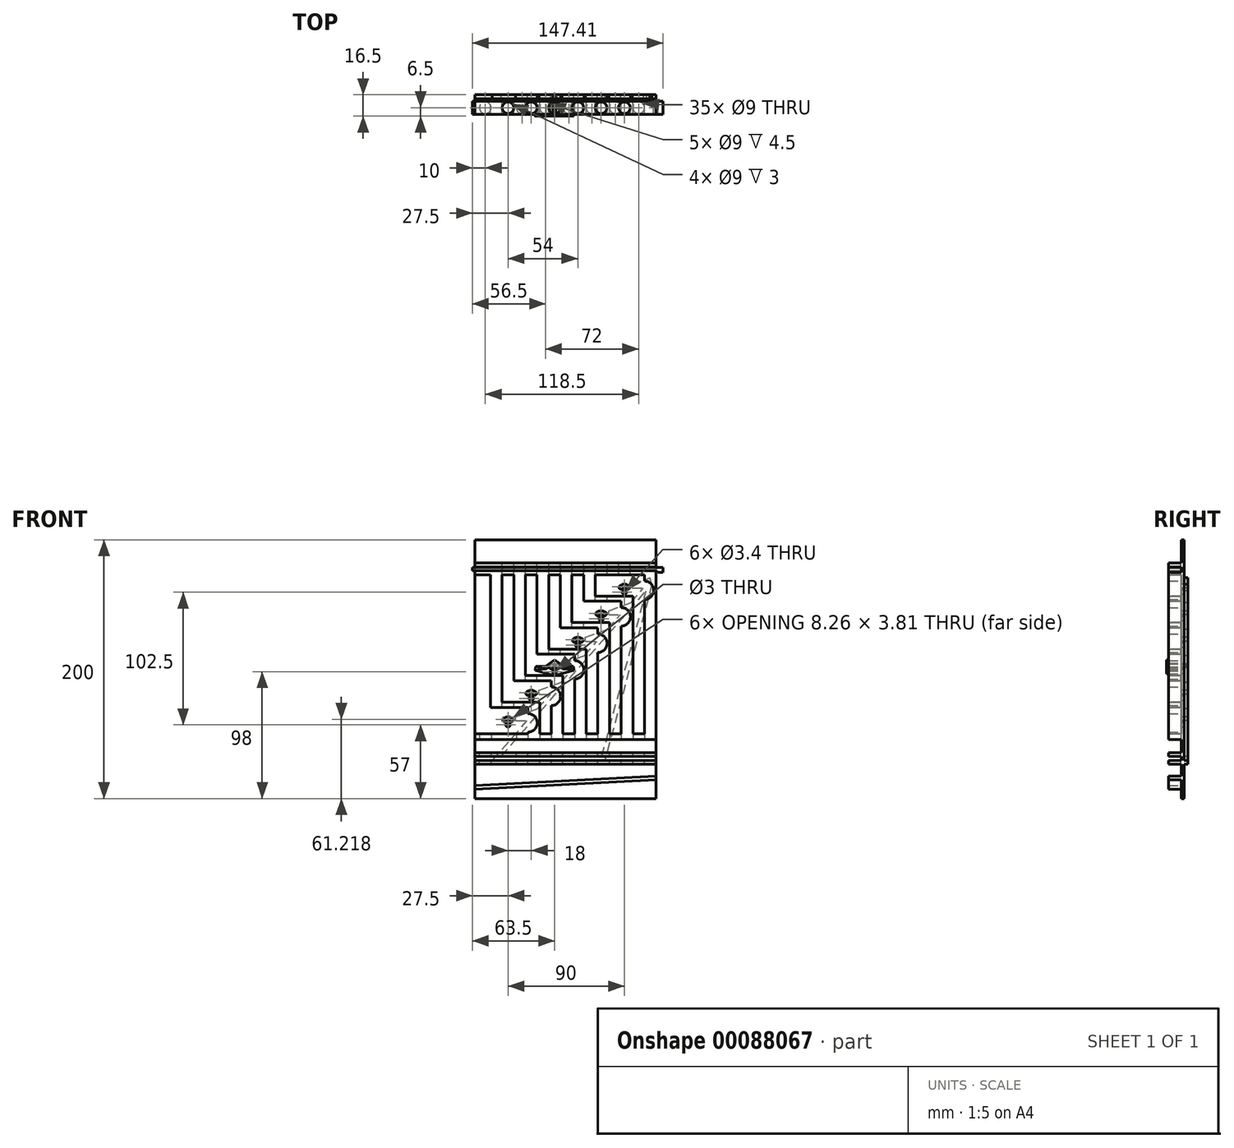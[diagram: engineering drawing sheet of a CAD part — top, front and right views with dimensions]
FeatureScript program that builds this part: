
annotation { "Feature Type Name" : "Feature", "Feature Type Description" : "" }
export const myFeature = defineFeature(function(context is Context, id is Id, definition is map)
    precondition{}
    {
        {
            var Q0;
            Q0=qCreatedBy(makeId("Front.planeOp"),FACE);
            var sketch = newSketch(context, id + "F0", { "sketchPlane" : qUnion([Q0])});
            skLineSegment(sketch, "E0.bottom", {"start": v(-70, 100) * mm, "end": v(70, 100) * mm});
            skLineSegment(sketch, "E0.top", {"start": v(-70, -100) * mm, "end": v(70, -100) * mm});
            skLineSegment(sketch, "E0.left", {"start": v(-70, 100) * mm, "end": v(-70, -100) * mm});
            skLineSegment(sketch, "E0.right", {"start": v(70, 100) * mm, "end": v(70, -100) * mm});
            skPoint(sketch, "E0.middle", {"position": v(0, 0) * mm});
            skSolve(sketch);
        }
        {
            var Q0;
            Q0=makeQuery(id+"F0.imprint","IMPRINT",FACE,{"disambiguationData":[TD([[makeQuery(id+"F0.imprint","IMPRINT",EDGE,{"derivedFrom":sQuery(id+"F0.wireOp",EDGE,"E0.bottom")}),-1.0]])]});
            extrude(context, id + "F1", {"entities" : qUnion([Q0]), "oppositeDirection" : true, "depth" : 2 * mm});
        }
        {
            var Q0;
            Q0=makeQuery(id+"F1.opExtrude","CAP_FACE",FACE,{"disambiguationData":[OSD([sQuery(id+"F0.wireOp",EDGE,"E0.bottom"),sQuery(id+"F0.wireOp",EDGE,"E0.top"),sQuery(id+"F0.wireOp",EDGE,"E0.left"),sQuery(id+"F0.wireOp",EDGE,"E0.right")])],"isStart":true});
            var sketch = newSketch(context, id + "F2", { "sketchPlane" : qUnion([Q0])});
            skLineSegment(sketch, "E1", {"start": v(70, -50) * mm, "end": v(61, -50) * mm});
            skLineSegment(sketch, "E2.1.0.0", {"start": v(61, -50) * mm, "end": v(52, -50) * mm});
            skLineSegment(sketch, "E2.2.0.0", {"start": v(52, -50) * mm, "end": v(43, -50) * mm});
            skLineSegment(sketch, "E2.3.0.0", {"start": v(43, -50) * mm, "end": v(34, -50) * mm});
            skLineSegment(sketch, "E2.4.0.0", {"start": v(34, -50) * mm, "end": v(25, -50) * mm});
            skLineSegment(sketch, "E2.5.0.0", {"start": v(25, -50) * mm, "end": v(16, -50) * mm});
            skLineSegment(sketch, "E2.6.0.0", {"start": v(16, -50) * mm, "end": v(7, -50) * mm});
            skLineSegment(sketch, "E2.7.0.0", {"start": v(7, -50) * mm, "end": v(-2, -50) * mm});
            skLineSegment(sketch, "E2.8.0.0", {"start": v(-2, -50) * mm, "end": v(-11, -50) * mm});
            skLineSegment(sketch, "E2.9.0.0", {"start": v(-11, -50) * mm, "end": v(-20, -50) * mm});
            skLineSegment(sketch, "E2.10.0.0", {"start": v(-20, -50) * mm, "end": v(-29, -50) * mm});
            skLineSegment(sketch, "E2.11.0.0", {"start": v(-29, -50) * mm, "end": v(-38, -50) * mm});
            skLineSegment(sketch, "E2.direction1", {"start": v(61, -50) * mm, "end": v(52, -50) * mm, "construction": true});
            skLineSegment(sketch, "E3", {"start": v(-38, -50) * mm, "end": v(70, 73) * mm, "construction": true});
            skLineSegment(sketch, "E4", {"start": v(-20, -50) * mm, "end": v(-20, -29.5) * mm});
            skLineSegment(sketch, "E5", {"start": v(-20, -29.5) * mm, "end": v(-29, -29.5) * mm});
            skLineSegment(sketch, "E6", {"start": v(-29, -29.5) * mm, "end": v(-29, -34.35) * mm});
            skLineSegment(sketch, "E7", {"start": v(-2, -50) * mm, "end": v(-2, -9) * mm});
            skLineSegment(sketch, "E8", {"start": v(-2, -9) * mm, "end": v(-11, -9) * mm});
            skLineSegment(sketch, "E9", {"start": v(-11, -9) * mm, "end": v(-11, -13.85) * mm});
            skLineSegment(sketch, "E10", {"start": v(16, -50) * mm, "end": v(16, 11.5) * mm});
            skLineSegment(sketch, "E11", {"start": v(16, 11.5) * mm, "end": v(7, 11.5) * mm});
            skLineSegment(sketch, "E12", {"start": v(7, 11.5) * mm, "end": v(7, 6.65) * mm});
            skLineSegment(sketch, "E13", {"start": v(34, -50) * mm, "end": v(34, 32) * mm});
            skLineSegment(sketch, "E14", {"start": v(34, 32) * mm, "end": v(25, 32) * mm});
            skLineSegment(sketch, "E15", {"start": v(25, 32) * mm, "end": v(25, 27.15) * mm});
            skLineSegment(sketch, "E16", {"start": v(52, -50) * mm, "end": v(52, 52.5) * mm});
            skLineSegment(sketch, "E17", {"start": v(52, 52.5) * mm, "end": v(43, 52.5) * mm});
            skLineSegment(sketch, "E18", {"start": v(43, 52.5) * mm, "end": v(43, 47.65) * mm});
            skLineSegment(sketch, "E19", {"start": v(70, -50) * mm, "end": v(70, 73) * mm});
            skLineSegment(sketch, "E20", {"start": v(70, 73) * mm, "end": v(61, 73) * mm});
            skLineSegment(sketch, "E21", {"start": v(61, 73) * mm, "end": v(61, 68.15) * mm});
            skArc(sketch, "E22", {"start": v(-29, -48.65) * mm, "mid": v(-21.85, -41.5) * mm, "end": v(-29, -34.35) * mm});
            skLineSegment(sketch, "E23.trimOffspring", {"start": v(-29, -48.65) * mm, "end": v(-29, -50) * mm});
            skArc(sketch, "E24.1.0.0", {"start": v(-11, -28.15) * mm, "mid": v(-3.85, -21) * mm, "end": v(-11, -13.85) * mm});
            skArc(sketch, "E24.2.0.0", {"start": v(7, -7.65) * mm, "mid": v(14.15, -0.5) * mm, "end": v(7, 6.65) * mm});
            skArc(sketch, "E24.3.0.0", {"start": v(25, 12.85) * mm, "mid": v(32.15, 20) * mm, "end": v(25, 27.15) * mm});
            skArc(sketch, "E24.4.0.0", {"start": v(43, 33.35) * mm, "mid": v(50.15, 40.5) * mm, "end": v(43, 47.65) * mm});
            skArc(sketch, "E24.5.0.0", {"start": v(61, 53.85) * mm, "mid": v(68.15, 61) * mm, "end": v(61, 68.15) * mm});
            skLineSegment(sketch, "E24.direction1", {"start": v(-29, -48.65) * mm, "end": v(-11, -28.15) * mm, "construction": true});
            skPoint(sketch, "E25", {"position": v(-11, -28.15) * mm});
            skLineSegment(sketch, "E26.trimOffspring", {"start": v(-11, -28.15) * mm, "end": v(-11, -50) * mm});
            skLineSegment(sketch, "E27.trimOffspring", {"start": v(7, -7.65) * mm, "end": v(7, -50) * mm});
            skLineSegment(sketch, "E28.trimOffspring", {"start": v(61, 53.85) * mm, "end": v(61, -50) * mm});
            skLineSegment(sketch, "E29.trimOffspring", {"start": v(43, 33.35) * mm, "end": v(43, -50) * mm});
            skLineSegment(sketch, "E30.trimOffspring", {"start": v(25, 12.85) * mm, "end": v(25, -50) * mm});
            skLineSegment(sketch, "E31.bottom", {"start": v(52, 52.5) * mm, "end": v(14, 52.5) * mm});
            skLineSegment(sketch, "E31.top", {"start": v(52, 56.5) * mm, "end": v(14, 56.5) * mm});
            skLineSegment(sketch, "E31.left", {"start": v(52, 52.5) * mm, "end": v(52, 56.5) * mm});
            skLineSegment(sketch, "E31.right", {"start": v(14, 52.5) * mm, "end": v(14, 56.5) * mm});
            skLineSegment(sketch, "E32.1.0.0", {"start": v(34, 32) * mm, "end": v(-4, 32) * mm});
            skLineSegment(sketch, "E32.1.0.1", {"start": v(34, 32) * mm, "end": v(34, 36) * mm});
            skLineSegment(sketch, "E32.1.0.2", {"start": v(34, 36) * mm, "end": v(-4, 36) * mm});
            skLineSegment(sketch, "E32.1.0.3", {"start": v(-4, 32) * mm, "end": v(-4, 36) * mm});
            skLineSegment(sketch, "E32.2.0.0", {"start": v(16, 11.5) * mm, "end": v(-22, 11.5) * mm});
            skLineSegment(sketch, "E32.2.0.1", {"start": v(16, 11.5) * mm, "end": v(16, 15.5) * mm});
            skLineSegment(sketch, "E32.2.0.2", {"start": v(16, 15.5) * mm, "end": v(-22, 15.5) * mm});
            skLineSegment(sketch, "E32.2.0.3", {"start": v(-22, 11.5) * mm, "end": v(-22, 15.5) * mm});
            skLineSegment(sketch, "E32.3.0.0", {"start": v(-2, -9) * mm, "end": v(-40, -9) * mm});
            skLineSegment(sketch, "E32.3.0.1", {"start": v(-2, -9) * mm, "end": v(-2, -5) * mm});
            skLineSegment(sketch, "E32.3.0.2", {"start": v(-2, -5) * mm, "end": v(-40, -5) * mm});
            skLineSegment(sketch, "E32.3.0.3", {"start": v(-40, -9) * mm, "end": v(-40, -5) * mm});
            skLineSegment(sketch, "E32.4.0.0", {"start": v(-20, -29.5) * mm, "end": v(-58, -29.5) * mm});
            skLineSegment(sketch, "E32.4.0.1", {"start": v(-20, -29.5) * mm, "end": v(-20, -25.5) * mm});
            skLineSegment(sketch, "E32.4.0.2", {"start": v(-20, -25.5) * mm, "end": v(-58, -25.5) * mm});
            skLineSegment(sketch, "E32.4.0.3", {"start": v(-58, -29.5) * mm, "end": v(-58, -25.5) * mm});
            skLineSegment(sketch, "E32.direction1", {"start": v(14, 52.5) * mm, "end": v(-4, 32) * mm, "construction": true});
            skLineSegment(sketch, "E33", {"start": v(61, 73) * mm, "end": v(-70, 73) * mm});
            skLineSegment(sketch, "E34", {"start": v(14, 56.5) * mm, "end": v(14, 73) * mm});
            skLineSegment(sketch, "E35", {"start": v(-4, 36) * mm, "end": v(-4, 73) * mm});
            skLineSegment(sketch, "E36", {"start": v(-22, 15.5) * mm, "end": v(-22, 73) * mm});
            skLineSegment(sketch, "E37", {"start": v(-40, -5) * mm, "end": v(-40, 73) * mm});
            skLineSegment(sketch, "E38", {"start": v(-58, -25.5) * mm, "end": v(-58, 73) * mm});
            skLineSegment(sketch, "E39", {"start": v(23, 73) * mm, "end": v(23, 56.5) * mm});
            skLineSegment(sketch, "E40", {"start": v(23, 56.5) * mm, "end": v(-49, -25.5) * mm, "construction": true});
            skLineSegment(sketch, "E41", {"start": v(5, 36) * mm, "end": v(5, 73) * mm});
            skLineSegment(sketch, "E42", {"start": v(-13, 15.5) * mm, "end": v(-13, 73) * mm});
            skLineSegment(sketch, "E43", {"start": v(-31, -5) * mm, "end": v(-31, 73) * mm});
            skLineSegment(sketch, "E44", {"start": v(-49, -25.5) * mm, "end": v(-49, 73) * mm});
            skLineSegment(sketch, "E45", {"start": v(-38, -50) * mm, "end": v(-70, -50) * mm});
            skLineSegment(sketch, "E46", {"start": v(-70, -54.5) * mm, "end": v(70, -54.5) * mm});
            skLineSegment(sketch, "E47", {"start": v(70, 76) * mm, "end": v(-70, 76) * mm});
            skLineSegment(sketch, "E48.bottom", {"start": v(-70, -50) * mm, "end": v(-38, -50) * mm});
            skLineSegment(sketch, "E48.top", {"start": v(-70, -46) * mm, "end": v(-38, -46) * mm});
            skLineSegment(sketch, "E48.left", {"start": v(-70, -50) * mm, "end": v(-70, -46) * mm});
            skLineSegment(sketch, "E48.right", {"start": v(-38, -50) * mm, "end": v(-38, -46) * mm});
            skPoint(sketch, "E49", {"position": v(-34.5, -25.5) * mm});
            skPoint(sketch, "E50", {"position": v(37.5, 56.5) * mm});
            skLineSegment(sketch, "E51.bottom", {"start": v(-70, -46) * mm, "end": v(-66.5, -46) * mm});
            skLineSegment(sketch, "E51.top", {"start": v(-70, -39) * mm, "end": v(-66.5, -39) * mm});
            skLineSegment(sketch, "E51.left", {"start": v(-70, -46) * mm, "end": v(-70, -39) * mm});
            skLineSegment(sketch, "E51.right", {"start": v(-66.5, -46) * mm, "end": v(-66.5, -39) * mm});
            skLineSegment(sketch, "E52.bottom", {"start": v(70, 82) * mm, "end": v(-70, 82) * mm});
            skLineSegment(sketch, "E52.top", {"start": v(70, 79) * mm, "end": v(-70, 79) * mm});
            skLineSegment(sketch, "E52.left", {"start": v(70, 82) * mm, "end": v(70, 79) * mm});
            skLineSegment(sketch, "E52.right", {"start": v(-70, 82) * mm, "end": v(-70, 79) * mm});
            skLineSegment(sketch, "E53.bottom", {"start": v(70, -64.5) * mm, "end": v(-70, -64.5) * mm});
            skLineSegment(sketch, "E53.top", {"start": v(70, -67.5) * mm, "end": v(-70, -67.5) * mm});
            skLineSegment(sketch, "E53.left", {"start": v(70, -64.5) * mm, "end": v(70, -67.5) * mm});
            skLineSegment(sketch, "E53.right", {"start": v(-70, -64.5) * mm, "end": v(-70, -67.5) * mm});
            skLineSegment(sketch, "E54", {"start": v(70, -82.5) * mm, "end": v(-70, -89.84) * mm});
            skLineSegment(sketch, "E55", {"start": v(-70, -92.84) * mm, "end": v(70, -85.5) * mm});
            skLineSegment(sketch, "E56", {"start": v(70, -82.5) * mm, "end": v(41.22, -82.5) * mm, "construction": true});
            skLineSegment(sketch, "E57.bottom", {"start": v(70, -70.5) * mm, "end": v(-70, -70.5) * mm});
            skLineSegment(sketch, "E57.top", {"start": v(70, -73.5) * mm, "end": v(-70, -73.5) * mm});
            skLineSegment(sketch, "E57.left", {"start": v(70, -70.5) * mm, "end": v(70, -73.5) * mm});
            skLineSegment(sketch, "E57.right", {"start": v(-70, -70.5) * mm, "end": v(-70, -73.5) * mm});
            skSolve(sketch);
        }
        {
            var Q0;
            {var subQ7=sQuery(id+"F2.wireOp",EDGE,"E20");Q0=makeQuery(id+"F2.imprint","IMPRINT",FACE,{"disambiguationData":[TD([[makeQuery(id+"F2.imprint","IMPRINT",EDGE,{"derivedFrom":subQ7}),-1.0]])]});}
            var Q1;
            Q1=makeQuery(id+"F2.imprint","IMPRINT",FACE,{"disambiguationData":[TD([[makeQuery(id+"F2.imprint","IMPRINT",EDGE,{"derivedFrom":sQuery(id+"F2.wireOp",EDGE,"E1")}),-1.0]])]});
            var Q2;
            Q2=makeQuery(id+"F2.imprint","IMPRINT",FACE,{"disambiguationData":[TD([[makeQuery(id+"F2.imprint","IMPRINT",EDGE,{"derivedFrom":sQuery(id+"F2.wireOp",EDGE,"E2.2.0.0")}),-1.0]])]});
            var Q3;
            Q3=makeQuery(id+"F2.imprint","IMPRINT",FACE,{"disambiguationData":[TD([[makeQuery(id+"F2.imprint","IMPRINT",EDGE,{"derivedFrom":sQuery(id+"F2.wireOp",EDGE,"E2.4.0.0")}),-1.0]])]});
            var Q4;
            Q4=makeQuery(id+"F2.imprint","IMPRINT",FACE,{"disambiguationData":[TD([[makeQuery(id+"F2.imprint","IMPRINT",EDGE,{"derivedFrom":sQuery(id+"F2.wireOp",EDGE,"E2.6.0.0")}),-1.0]])]});
            var Q5;
            Q5=makeQuery(id+"F2.imprint","IMPRINT",FACE,{"disambiguationData":[TD([[makeQuery(id+"F2.imprint","IMPRINT",EDGE,{"derivedFrom":sQuery(id+"F2.wireOp",EDGE,"E2.8.0.0")}),-1.0]])]});
            var Q6;
            Q6=makeQuery(id+"F2.imprint","IMPRINT",FACE,{"disambiguationData":[TD([[makeQuery(id+"F2.imprint","IMPRINT",EDGE,{"derivedFrom":sQuery(id+"F2.wireOp",EDGE,"E2.10.0.0")}),-1.0]])]});
            var Q7;
            {var subQ0=sQuery(id+"F2.wireOp",EDGE,"E1");Q7=makeQuery(id+"F2.imprint","IMPRINT",FACE,{"disambiguationData":[TD([[makeQuery(id+"F2.imprint","IMPRINT",EDGE,{"derivedFrom":subQ0}),1.0]])]});}
            var Q8;
            Q8=makeQuery(id+"F2.imprint","IMPRINT",FACE,{"disambiguationData":[TD([[makeQuery(id+"F2.imprint","IMPRINT",EDGE,{"derivedFrom":sQuery(id+"F2.wireOp",EDGE,"E48.bottom")}),1.0]])]});
            var Q9;
            {var subQ1=sQuery(id+"F2.wireOp",EDGE,"E32.4.0.1");Q9=makeQuery(id+"F2.imprint","IMPRINT",FACE,{"disambiguationData":[TD([[makeQuery(id+"F2.imprint","IMPRINT",EDGE,{"derivedFrom":subQ1}),1.0]])]});}
            var Q10;
            {var subQ1=sQuery(id+"F2.wireOp",EDGE,"E32.3.0.1");Q10=makeQuery(id+"F2.imprint","IMPRINT",FACE,{"disambiguationData":[TD([[makeQuery(id+"F2.imprint","IMPRINT",EDGE,{"derivedFrom":subQ1}),1.0]])]});}
            var Q11;
            {var subQ1=sQuery(id+"F2.wireOp",EDGE,"E32.2.0.1");Q11=makeQuery(id+"F2.imprint","IMPRINT",FACE,{"disambiguationData":[TD([[makeQuery(id+"F2.imprint","IMPRINT",EDGE,{"derivedFrom":subQ1}),1.0]])]});}
            var Q12;
            {var subQ1=sQuery(id+"F2.wireOp",EDGE,"E32.1.0.1");Q12=makeQuery(id+"F2.imprint","IMPRINT",FACE,{"disambiguationData":[TD([[makeQuery(id+"F2.imprint","IMPRINT",EDGE,{"derivedFrom":subQ1}),1.0]])]});}
            var Q13;
            {var subQ3=sQuery(id+"F2.wireOp",EDGE,"E31.left");Q13=makeQuery(id+"F2.imprint","IMPRINT",FACE,{"disambiguationData":[TD([[makeQuery(id+"F2.imprint","IMPRINT",EDGE,{"derivedFrom":subQ3}),1.0]])]});}
            var Q14;
            {var subQ0=sQuery(id+"F2.wireOp",EDGE,"E34");Q14=makeQuery(id+"F2.imprint","IMPRINT",FACE,{"disambiguationData":[TD([[makeQuery(id+"F2.imprint","IMPRINT",EDGE,{"derivedFrom":subQ0}),-1.0]])]});}
            var Q15;
            {var subQ0=sQuery(id+"F2.wireOp",EDGE,"E35");Q15=makeQuery(id+"F2.imprint","IMPRINT",FACE,{"disambiguationData":[TD([[makeQuery(id+"F2.imprint","IMPRINT",EDGE,{"derivedFrom":subQ0}),-1.0]])]});}
            var Q16;
            {var subQ0=sQuery(id+"F2.wireOp",EDGE,"E36");Q16=makeQuery(id+"F2.imprint","IMPRINT",FACE,{"disambiguationData":[TD([[makeQuery(id+"F2.imprint","IMPRINT",EDGE,{"derivedFrom":subQ0}),-1.0]])]});}
            var Q17;
            {var subQ0=sQuery(id+"F2.wireOp",EDGE,"E37");Q17=makeQuery(id+"F2.imprint","IMPRINT",FACE,{"disambiguationData":[TD([[makeQuery(id+"F2.imprint","IMPRINT",EDGE,{"derivedFrom":subQ0}),-1.0]])]});}
            var Q18;
            {var subQ0=sQuery(id+"F2.wireOp",EDGE,"E38");Q18=makeQuery(id+"F2.imprint","IMPRINT",FACE,{"disambiguationData":[TD([[makeQuery(id+"F2.imprint","IMPRINT",EDGE,{"derivedFrom":subQ0}),-1.0]])]});}
            var Q19;
            Q19=makeQuery(id+"F2.imprint","IMPRINT",FACE,{"disambiguationData":[TD([[makeQuery(id+"F2.imprint","IMPRINT",EDGE,{"derivedFrom":sQuery(id+"F2.wireOp",EDGE,"E51.bottom")}),1.0]])]});
            var Q20;
            Q20=makeQuery(id+"F2.imprint","IMPRINT",FACE,{"disambiguationData":[TD([[makeQuery(id+"F2.imprint","IMPRINT",EDGE,{"derivedFrom":sQuery(id+"F2.wireOp",EDGE,"E52.bottom")}),1.0]])]});
            var Q21;
            Q21=makeQuery(id+"F2.imprint","IMPRINT",FACE,{"disambiguationData":[TD([[makeQuery(id+"F2.imprint","IMPRINT",EDGE,{"derivedFrom":sQuery(id+"F2.wireOp",EDGE,"E53.bottom")}),1.0]])]});
            var Q22;
            {var subQ0=sQuery(id+"F2.wireOp",EDGE,"E54");Q22=makeQuery(id+"F2.imprint","IMPRINT",FACE,{"disambiguationData":[TD([[makeQuery(id+"F2.imprint","IMPRINT",EDGE,{"derivedFrom":subQ0}),1.0]])]});}
            var Q23;
            Q23=makeQuery(id+"F2.imprint","IMPRINT",FACE,{"disambiguationData":[TD([[makeQuery(id+"F2.imprint","IMPRINT",EDGE,{"derivedFrom":sQuery(id+"F2.wireOp",EDGE,"E57.bottom")}),1.0]])]});
            extrude(context, id + "F3", {"entities" : qUnion([Q0, Q1, Q2, Q3, Q4, Q5, Q6, Q7, Q8, Q9, Q10, Q11, Q12, Q13, Q14, Q15, Q16, Q17, Q18, Q19, Q20, Q21, Q22, Q23]), "operationType" : NewBodyOperationType.ADD, "depth" : 10 * mm});
        }
        {
            var Q0;
            Q0=makeQuery(id+"F3.opExtrude","CAP_FACE",FACE,{"disambiguationData":[OSD([sQuery(id+"F0.wireOp",EDGE,"E0.left"),sQuery(id+"F0.wireOp",EDGE,"E0.right"),sQuery(id+"F2.wireOp",EDGE,"E2.1.0.0"),sQuery(id+"F2.wireOp",EDGE,"E2.3.0.0"),sQuery(id+"F2.wireOp",EDGE,"E2.5.0.0"),sQuery(id+"F2.wireOp",EDGE,"E2.7.0.0"),sQuery(id+"F2.wireOp",EDGE,"E2.9.0.0"),sQuery(id+"F2.wireOp",EDGE,"E2.11.0.0"),sQuery(id+"F2.wireOp",EDGE,"E4"),sQuery(id+"F2.wireOp",EDGE,"E6"),sQuery(id+"F2.wireOp",EDGE,"E7"),sQuery(id+"F2.wireOp",EDGE,"E9"),sQuery(id+"F2.wireOp",EDGE,"E10"),sQuery(id+"F2.wireOp",EDGE,"E12"),sQuery(id+"F2.wireOp",EDGE,"E13"),sQuery(id+"F2.wireOp",EDGE,"E15"),sQuery(id+"F2.wireOp",EDGE,"E16"),sQuery(id+"F2.wireOp",EDGE,"E18"),sQuery(id+"F2.wireOp",EDGE,"E19"),sQuery(id+"F2.wireOp",EDGE,"E21"),sQuery(id+"F2.wireOp",EDGE,"E22"),sQuery(id+"F2.wireOp",EDGE,"E23.trimOffspring"),sQuery(id+"F2.wireOp",EDGE,"E24.1.0.0"),sQuery(id+"F2.wireOp",EDGE,"E24.2.0.0"),sQuery(id+"F2.wireOp",EDGE,"E24.3.0.0"),sQuery(id+"F2.wireOp",EDGE,"E24.4.0.0"),sQuery(id+"F2.wireOp",EDGE,"E24.5.0.0"),sQuery(id+"F2.wireOp",EDGE,"E26.trimOffspring"),sQuery(id+"F2.wireOp",EDGE,"E27.trimOffspring"),sQuery(id+"F2.wireOp",EDGE,"E28.trimOffspring"),sQuery(id+"F2.wireOp",EDGE,"E29.trimOffspring"),sQuery(id+"F2.wireOp",EDGE,"E30.trimOffspring"),sQuery(id+"F2.wireOp",EDGE,"E31.bottom"),sQuery(id+"F2.wireOp",EDGE,"E31.top"),sQuery(id+"F2.wireOp",EDGE,"E31.left"),sQuery(id+"F2.wireOp",EDGE,"E31.right"),sQuery(id+"F2.wireOp",EDGE,"E32.1.0.0"),sQuery(id+"F2.wireOp",EDGE,"E32.1.0.1"),sQuery(id+"F2.wireOp",EDGE,"E32.1.0.2"),sQuery(id+"F2.wireOp",EDGE,"E32.1.0.3"),sQuery(id+"F2.wireOp",EDGE,"E32.2.0.0"),sQuery(id+"F2.wireOp",EDGE,"E32.2.0.1"),sQuery(id+"F2.wireOp",EDGE,"E32.2.0.2"),sQuery(id+"F2.wireOp",EDGE,"E32.2.0.3"),sQuery(id+"F2.wireOp",EDGE,"E32.3.0.0"),sQuery(id+"F2.wireOp",EDGE,"E32.3.0.1"),sQuery(id+"F2.wireOp",EDGE,"E32.3.0.2"),sQuery(id+"F2.wireOp",EDGE,"E32.3.0.3"),sQuery(id+"F2.wireOp",EDGE,"E32.4.0.0"),sQuery(id+"F2.wireOp",EDGE,"E32.4.0.1"),sQuery(id+"F2.wireOp",EDGE,"E32.4.0.2"),sQuery(id+"F2.wireOp",EDGE,"E32.4.0.3"),sQuery(id+"F2.wireOp",EDGE,"E33"),sQuery(id+"F2.wireOp",EDGE,"E34"),sQuery(id+"F2.wireOp",EDGE,"E35"),sQuery(id+"F2.wireOp",EDGE,"E36"),sQuery(id+"F2.wireOp",EDGE,"E37"),sQuery(id+"F2.wireOp",EDGE,"E38"),sQuery(id+"F2.wireOp",EDGE,"E39"),sQuery(id+"F2.wireOp",EDGE,"E41"),sQuery(id+"F2.wireOp",EDGE,"E42"),sQuery(id+"F2.wireOp",EDGE,"E43"),sQuery(id+"F2.wireOp",EDGE,"E44"),sQuery(id+"F2.wireOp",EDGE,"E46"),sQuery(id+"F2.wireOp",EDGE,"E47"),sQuery(id+"F2.wireOp",EDGE,"E48.top"),sQuery(id+"F2.wireOp",EDGE,"E48.left"),sQuery(id+"F2.wireOp",EDGE,"E48.right")])],"isStart":false});
            var sketch = newSketch(context, id + "F4", { "sketchPlane" : qUnion([Q0])});
            skPoint(sketch, "E58.0", {"position": v(-34.5, -25.5) * mm});
            skSolve(sketch);
        }
        {
            var Q0;
            Q0=sQuery(id+"F2.wireOp",VERTEX,"E49");
            var Q1;
            Q1=sQuery(id+"F2.wireOp",VERTEX,"E50");
            var Q2;
            Q2=sQuery(id+"F4.wireOp",VERTEX,"E58.0");
            cPlane(context, id + "F5", {"entities" : qUnion([Q0, Q1, Q2]), "cplaneType" : CPlaneType.THREE_POINT, "offset" : 150 * mm, "width" : 150 * mm, "height" : 150 * mm});
        }
        {
            var Q0;
            Q0=makeQuery(id+"F3.opExtrude","SWEPT_FACE",FACE,{"disambiguationData":[OSD([sQuery(id+"F2.wireOp",EDGE,"E47")])]});
            var sketch = newSketch(context, id + "F6", { "sketchPlane" : qUnion([Q0])});
            skLineSegment(sketch, "E59.0.0", {"start": v(-49, 0) * mm, "end": v(-40, 0) * mm});
            skLineSegment(sketch, "E59.0.1", {"start": v(-40, 0) * mm, "end": v(-40, -10) * mm});
            skLineSegment(sketch, "E59.0.2", {"start": v(-40, -10) * mm, "end": v(-49, -10) * mm});
            skLineSegment(sketch, "E59.0.3", {"start": v(-49, -10) * mm, "end": v(-49, 0) * mm});
            skCircle(sketch, "E60", {"center": v(-44.5, -5) * mm, "radius": 4.5 * mm});
            skPoint(sketch, "E60.centerSnap0", {"position": v(-44.5, -10) * mm});
            skPoint(sketch, "E60.centerSnap1", {"position": v(-40, -5) * mm});
            skCircle(sketch, "E61.1.0.0", {"center": v(-26.5, -5) * mm, "radius": 4.5 * mm});
            skCircle(sketch, "E61.2.0.0", {"center": v(-8.5, -5) * mm, "radius": 4.5 * mm});
            skCircle(sketch, "E61.3.0.0", {"center": v(9.5, -5) * mm, "radius": 4.5 * mm});
            skCircle(sketch, "E61.4.0.0", {"center": v(27.5, -5) * mm, "radius": 4.5 * mm});
            skCircle(sketch, "E61.5.0.0", {"center": v(45.5, -5) * mm, "radius": 4.5 * mm});
            skLineSegment(sketch, "E61.direction1", {"start": v(-44.5, -5) * mm, "end": v(-26.5, -5) * mm, "construction": true});
            skSolve(sketch);
        }
        {
            var Q0;
            {var subQ0=sQuery(id+"F6.wireOp",EDGE,"E60");var subQ1=makeQuery(id+"F6.imprint","INTERSECT",VERTEX,{"derivedFrom":[sQuery(id+"F6.wireOp",EDGE,"E59.0.1"),subQ0]});Q0=makeQuery(id+"F6.imprint","IMPRINT",FACE,{"disambiguationData":[TD([[makeQuery(id+"F6.imprint","IMPRINT",EDGE,{"disambiguationData":[TD([[subQ1,-1.0]])],"derivedFrom":subQ0}),1.0]])]});}
            var Q1;
            Q1=makeQuery(id+"F6.imprint","IMPRINT",FACE,{"disambiguationData":[TD([[makeQuery(id+"F6.imprint","IMPRINT",EDGE,{"derivedFrom":sQuery(id+"F6.wireOp",EDGE,"E61.1.0.0")}),1.0]])]});
            var Q2;
            Q2=makeQuery(id+"F6.imprint","IMPRINT",FACE,{"disambiguationData":[TD([[makeQuery(id+"F6.imprint","IMPRINT",EDGE,{"derivedFrom":sQuery(id+"F6.wireOp",EDGE,"E61.2.0.0")}),1.0]])]});
            var Q3;
            Q3=makeQuery(id+"F6.imprint","IMPRINT",FACE,{"disambiguationData":[TD([[makeQuery(id+"F6.imprint","IMPRINT",EDGE,{"derivedFrom":sQuery(id+"F6.wireOp",EDGE,"E61.3.0.0")}),1.0]])]});
            var Q4;
            Q4=makeQuery(id+"F6.imprint","IMPRINT",FACE,{"disambiguationData":[TD([[makeQuery(id+"F6.imprint","IMPRINT",EDGE,{"derivedFrom":sQuery(id+"F6.wireOp",EDGE,"E61.4.0.0")}),1.0]])]});
            var Q5;
            Q5=makeQuery(id+"F6.imprint","IMPRINT",FACE,{"disambiguationData":[TD([[makeQuery(id+"F6.imprint","IMPRINT",EDGE,{"derivedFrom":sQuery(id+"F6.wireOp",EDGE,"E61.5.0.0")}),1.0]])]});
            var Q6;
            Q6=qCreatedBy(id+"F5.planeOp",FACE);
            var Q7;
            Q7=makeQuery(id+"F3.opExtrude","SWEPT_FACE",FACE,{"disambiguationData":[OSD([sQuery(id+"F2.wireOp",EDGE,"E52.bottom")])]});
            extrude(context, id + "F7", {"entities" : qUnion([Q0, Q1, Q2, Q3, Q4, Q5]), "operationType" : NewBodyOperationType.REMOVE, "endBound" : BoundingType.UP_TO_SURFACE, "oppositeDirection" : true, "endBoundEntityFace" : qUnion([Q6]), "depth" : 25 * mm, "hasSecondDirection" : true, "secondDirectionBound" : SecondDirectionBoundingType.UP_TO_SURFACE, "secondDirectionOppositeDirection" : false, "secondDirectionBoundEntityFace" : qUnion([Q7]), "secondDirectionDepth" : 25 * mm});
        }
        {
            var Q0;
            Q0=makeQuery(id+"F3.opExtrude","SWEPT_FACE",FACE,{"disambiguationData":[OSD([sQuery(id+"F2.wireOp",EDGE,"E46")])]});
            var sketch = newSketch(context, id + "F8", { "sketchPlane" : qUnion([Q0])});
            skLineSegment(sketch, "E62.0.0", {"start": v(-29, 0) * mm, "end": v(-38, 0) * mm});
            skLineSegment(sketch, "E62.0.1", {"start": v(-38, 0) * mm, "end": v(-38, 10) * mm});
            skLineSegment(sketch, "E62.0.2", {"start": v(-38, 10) * mm, "end": v(-29, 10) * mm});
            skLineSegment(sketch, "E62.0.3", {"start": v(-29, 10) * mm, "end": v(-29, 0) * mm});
            skCircle(sketch, "E63", {"center": v(-33.5, 5) * mm, "radius": 4.5 * mm});
            skPoint(sketch, "E63.centerSnap0", {"position": v(-33.5, 10) * mm});
            skPoint(sketch, "E63.centerSnap1", {"position": v(-38, 5) * mm});
            skCircle(sketch, "E64.1.0.0", {"center": v(-15.5, 5) * mm, "radius": 4.5 * mm});
            skCircle(sketch, "E64.2.0.0", {"center": v(2.5, 5) * mm, "radius": 4.5 * mm});
            skCircle(sketch, "E64.3.0.0", {"center": v(20.5, 5) * mm, "radius": 4.5 * mm});
            skCircle(sketch, "E64.4.0.0", {"center": v(38.5, 5) * mm, "radius": 4.5 * mm});
            skCircle(sketch, "E64.5.0.0", {"center": v(56.5, 5) * mm, "radius": 4.5 * mm});
            skLineSegment(sketch, "E64.direction1", {"start": v(-33.5, 5) * mm, "end": v(-15.5, 5) * mm, "construction": true});
            skCircle(sketch, "E65.1.0.0", {"center": v(-62, 5) * mm, "radius": 4.5 * mm});
            skLineSegment(sketch, "E65.direction1", {"start": v(-33.5, 5) * mm, "end": v(-62, 5) * mm, "construction": true});
            skSolve(sketch);
        }
        {
            var Q0;
            Q0=makeQuery(id+"F8.imprint","IMPRINT",FACE,{"disambiguationData":[TD([[makeQuery(id+"F8.imprint","IMPRINT",EDGE,{"derivedFrom":sQuery(id+"F8.wireOp",EDGE,"E65.1.0.0")}),1.0]])]});
            var Q1;
            {var subQ0=sQuery(id+"F8.wireOp",EDGE,"E63");var subQ1=makeQuery(id+"F8.imprint","INTERSECT",VERTEX,{"derivedFrom":[sQuery(id+"F8.wireOp",EDGE,"E62.0.1"),subQ0]});Q1=makeQuery(id+"F8.imprint","IMPRINT",FACE,{"disambiguationData":[TD([[makeQuery(id+"F8.imprint","IMPRINT",EDGE,{"disambiguationData":[TD([[subQ1,1.0]])],"derivedFrom":subQ0}),1.0]])]});}
            var Q2;
            Q2=makeQuery(id+"F8.imprint","IMPRINT",FACE,{"disambiguationData":[TD([[makeQuery(id+"F8.imprint","IMPRINT",EDGE,{"derivedFrom":sQuery(id+"F8.wireOp",EDGE,"E64.1.0.0")}),1.0]])]});
            var Q3;
            Q3=makeQuery(id+"F8.imprint","IMPRINT",FACE,{"disambiguationData":[TD([[makeQuery(id+"F8.imprint","IMPRINT",EDGE,{"derivedFrom":sQuery(id+"F8.wireOp",EDGE,"E64.2.0.0")}),1.0]])]});
            var Q4;
            Q4=makeQuery(id+"F8.imprint","IMPRINT",FACE,{"disambiguationData":[TD([[makeQuery(id+"F8.imprint","IMPRINT",EDGE,{"derivedFrom":sQuery(id+"F8.wireOp",EDGE,"E64.3.0.0")}),1.0]])]});
            var Q5;
            Q5=makeQuery(id+"F8.imprint","IMPRINT",FACE,{"disambiguationData":[TD([[makeQuery(id+"F8.imprint","IMPRINT",EDGE,{"derivedFrom":sQuery(id+"F8.wireOp",EDGE,"E64.4.0.0")}),1.0]])]});
            var Q6;
            Q6=makeQuery(id+"F8.imprint","IMPRINT",FACE,{"disambiguationData":[TD([[makeQuery(id+"F8.imprint","IMPRINT",EDGE,{"derivedFrom":sQuery(id+"F8.wireOp",EDGE,"E64.5.0.0")}),1.0]])]});
            extrude(context, id + "F9", {"entities" : qUnion([Q0, Q1, Q2, Q3, Q4, Q5, Q6]), "operationType" : NewBodyOperationType.REMOVE, "endBound" : BoundingType.UP_TO_NEXT, "oppositeDirection" : true, "depth" : 25 * mm});
        }
        {
            var Q0;
            Q0=makeQuery(id+"F2.imprint","IMPRINT",FACE,{"disambiguationData":[TD([[makeQuery(id+"F2.imprint","IMPRINT",EDGE,{"derivedFrom":sQuery(id+"F2.wireOp",EDGE,"E2.11.0.0")}),-1.0]])]});
            var sketch = newSketch(context, id + "F10", { "sketchPlane" : qUnion([Q0])});
            skLineSegment(sketch, "E66.0", {"start": v(-40, -25.5) * mm, "end": v(-49, -25.5) * mm});
            skLineSegment(sketch, "E67.0", {"start": v(-44.5, -46) * mm, "end": v(-38, -46) * mm});
            skLineSegment(sketch, "E68", {"start": v(-44.5, -46) * mm, "end": v(-44.5, -43) * mm, "construction": true});
            skPoint(sketch, "E68.startSnap0", {"position": v(-44.5, -25.5) * mm});
            skCircle(sketch, "E69", {"center": v(-44.5, -43) * mm, "radius": 1.7 * mm});
            skLineSegment(sketch, "E70", {"start": v(-42.7, -40.44) * mm, "end": v(-42.7, -40.44) * mm});
            skArc(sketch, "E71", {"start": v(-40.99, -37.98) * mm, "mid": v(-44.5, -36.88) * mm, "end": v(-48.01, -37.98) * mm});
            skLineSegment(sketch, "E72", {"start": v(-44.5, -43) * mm, "end": v(-44.5, -36.88) * mm, "construction": true});
            skLineSegment(sketch, "E73", {"start": v(-44.5, -43) * mm, "end": v(-46.3, -40.44) * mm, "construction": true});
            skLineSegment(sketch, "E74", {"start": v(-46.3, -40.44) * mm, "end": v(-47.15, -39.21) * mm});
            skArc(sketch, "E75", {"start": v(-42.7, -40.44) * mm, "mid": v(-44.5, -39.88) * mm, "end": v(-46.3, -40.44) * mm});
            skLineSegment(sketch, "E76", {"start": v(-44.5, -43) * mm, "end": v(-42.7, -40.44) * mm, "construction": true});
            skLineSegment(sketch, "E77", {"start": v(-41.85, -39.21) * mm, "end": v(-42.7, -40.44) * mm});
            skArc(sketch, "E78", {"start": v(-48.01, -37.98) * mm, "mid": v(-48.38, -40.07) * mm, "end": v(-46.3, -40.44) * mm});
            skArc(sketch, "E79", {"start": v(-42.7, -40.44) * mm, "mid": v(-40.62, -40.07) * mm, "end": v(-40.99, -37.98) * mm});
            skPoint(sketch, "E80.orphan", {"position": v(-70, -46) * mm});
            skPoint(sketch, "E81.1.0.0", {"position": v(-26.5, -22.5) * mm});
            skArc(sketch, "E81.1.0.1", {"start": v(-24.7, -19.94) * mm, "mid": v(-22.62, -19.57) * mm, "end": v(-22.99, -17.48) * mm});
            skArc(sketch, "E81.1.0.2", {"start": v(-30.01, -17.48) * mm, "mid": v(-30.38, -19.57) * mm, "end": v(-28.3, -19.94) * mm});
            skLineSegment(sketch, "E81.1.0.3", {"start": v(-23.85, -18.71) * mm, "end": v(-24.7, -19.94) * mm});
            skLineSegment(sketch, "E81.1.0.4", {"start": v(-26.5, -22.5) * mm, "end": v(-24.7, -19.94) * mm, "construction": true});
            skArc(sketch, "E81.1.0.5", {"start": v(-22.99, -17.48) * mm, "mid": v(-26.5, -16.38) * mm, "end": v(-30.01, -17.48) * mm});
            skCircle(sketch, "E81.1.0.6", {"center": v(-26.5, -22.5) * mm, "radius": 1.7 * mm});
            skArc(sketch, "E81.1.0.7", {"start": v(-24.7, -19.94) * mm, "mid": v(-26.5, -19.38) * mm, "end": v(-28.3, -19.94) * mm});
            skLineSegment(sketch, "E81.1.0.8", {"start": v(-26.5, -25.5) * mm, "end": v(-26.5, -22.5) * mm, "construction": true});
            skLineSegment(sketch, "E81.1.0.9", {"start": v(-26.5, -25.5) * mm, "end": v(-20, -25.5) * mm});
            skLineSegment(sketch, "E81.1.0.10", {"start": v(-28.3, -19.94) * mm, "end": v(-29.15, -18.71) * mm});
            skLineSegment(sketch, "E81.1.0.11", {"start": v(-26.5, -22.5) * mm, "end": v(-28.3, -19.94) * mm, "construction": true});
            skLineSegment(sketch, "E81.1.0.12", {"start": v(-26.5, -22.5) * mm, "end": v(-26.5, -16.38) * mm, "construction": true});
            skPoint(sketch, "E81.2.0.0", {"position": v(-8.5, -2) * mm});
            skArc(sketch, "E81.2.0.1", {"start": v(-6.7, 0.56) * mm, "mid": v(-4.62, 0.93) * mm, "end": v(-4.99, 3.02) * mm});
            skArc(sketch, "E81.2.0.2", {"start": v(-12.01, 3.02) * mm, "mid": v(-12.38, 0.93) * mm, "end": v(-10.3, 0.56) * mm});
            skLineSegment(sketch, "E81.2.0.3", {"start": v(-5.85, 1.79) * mm, "end": v(-6.7, 0.56) * mm});
            skLineSegment(sketch, "E81.2.0.4", {"start": v(-8.5, -2) * mm, "end": v(-6.7, 0.56) * mm, "construction": true});
            skArc(sketch, "E81.2.0.5", {"start": v(-4.99, 3.02) * mm, "mid": v(-8.5, 4.13) * mm, "end": v(-12.01, 3.02) * mm});
            skCircle(sketch, "E81.2.0.6", {"center": v(-8.5, -2) * mm, "radius": 1.7 * mm});
            skArc(sketch, "E81.2.0.7", {"start": v(-6.7, 0.56) * mm, "mid": v(-8.5, 1.13) * mm, "end": v(-10.3, 0.56) * mm});
            skLineSegment(sketch, "E81.2.0.8", {"start": v(-8.5, -5) * mm, "end": v(-8.5, -2) * mm, "construction": true});
            skLineSegment(sketch, "E81.2.0.9", {"start": v(-8.5, -5) * mm, "end": v(-2, -5) * mm});
            skLineSegment(sketch, "E81.2.0.10", {"start": v(-10.3, 0.56) * mm, "end": v(-11.15, 1.79) * mm});
            skLineSegment(sketch, "E81.2.0.11", {"start": v(-8.5, -2) * mm, "end": v(-10.3, 0.56) * mm, "construction": true});
            skLineSegment(sketch, "E81.2.0.12", {"start": v(-8.5, -2) * mm, "end": v(-8.5, 4.13) * mm, "construction": true});
            skPoint(sketch, "E81.3.0.0", {"position": v(9.5, 18.5) * mm});
            skArc(sketch, "E81.3.0.1", {"start": v(11.3, 21.06) * mm, "mid": v(13.38, 21.43) * mm, "end": v(13.01, 23.52) * mm});
            skArc(sketch, "E81.3.0.2", {"start": v(5.99, 23.52) * mm, "mid": v(5.62, 21.43) * mm, "end": v(7.7, 21.06) * mm});
            skLineSegment(sketch, "E81.3.0.3", {"start": v(12.15, 22.29) * mm, "end": v(11.3, 21.06) * mm});
            skLineSegment(sketch, "E81.3.0.4", {"start": v(9.5, 18.5) * mm, "end": v(11.3, 21.06) * mm, "construction": true});
            skArc(sketch, "E81.3.0.5", {"start": v(13.01, 23.52) * mm, "mid": v(9.5, 24.63) * mm, "end": v(5.99, 23.52) * mm});
            skCircle(sketch, "E81.3.0.6", {"center": v(9.5, 18.5) * mm, "radius": 1.7 * mm});
            skArc(sketch, "E81.3.0.7", {"start": v(11.3, 21.06) * mm, "mid": v(9.5, 21.63) * mm, "end": v(7.7, 21.06) * mm});
            skLineSegment(sketch, "E81.3.0.8", {"start": v(9.5, 15.5) * mm, "end": v(9.5, 18.5) * mm, "construction": true});
            skLineSegment(sketch, "E81.3.0.9", {"start": v(9.5, 15.5) * mm, "end": v(16, 15.5) * mm});
            skLineSegment(sketch, "E81.3.0.10", {"start": v(7.7, 21.06) * mm, "end": v(6.85, 22.29) * mm});
            skLineSegment(sketch, "E81.3.0.11", {"start": v(9.5, 18.5) * mm, "end": v(7.7, 21.06) * mm, "construction": true});
            skLineSegment(sketch, "E81.3.0.12", {"start": v(9.5, 18.5) * mm, "end": v(9.5, 24.63) * mm, "construction": true});
            skPoint(sketch, "E81.4.0.0", {"position": v(27.5, 39) * mm});
            skArc(sketch, "E81.4.0.1", {"start": v(29.3, 41.56) * mm, "mid": v(31.38, 41.93) * mm, "end": v(31.01, 44.02) * mm});
            skArc(sketch, "E81.4.0.2", {"start": v(23.99, 44.02) * mm, "mid": v(23.62, 41.93) * mm, "end": v(25.7, 41.56) * mm});
            skLineSegment(sketch, "E81.4.0.3", {"start": v(30.15, 42.79) * mm, "end": v(29.3, 41.56) * mm});
            skLineSegment(sketch, "E81.4.0.4", {"start": v(27.5, 39) * mm, "end": v(29.3, 41.56) * mm, "construction": true});
            skArc(sketch, "E81.4.0.5", {"start": v(31.01, 44.02) * mm, "mid": v(27.5, 45.13) * mm, "end": v(23.99, 44.02) * mm});
            skCircle(sketch, "E81.4.0.6", {"center": v(27.5, 39) * mm, "radius": 1.7 * mm});
            skArc(sketch, "E81.4.0.7", {"start": v(29.3, 41.56) * mm, "mid": v(27.5, 42.13) * mm, "end": v(25.7, 41.56) * mm});
            skLineSegment(sketch, "E81.4.0.8", {"start": v(27.5, 36) * mm, "end": v(27.5, 39) * mm, "construction": true});
            skLineSegment(sketch, "E81.4.0.9", {"start": v(27.5, 36) * mm, "end": v(34, 36) * mm});
            skLineSegment(sketch, "E81.4.0.10", {"start": v(25.7, 41.56) * mm, "end": v(24.85, 42.79) * mm});
            skLineSegment(sketch, "E81.4.0.11", {"start": v(27.5, 39) * mm, "end": v(25.7, 41.56) * mm, "construction": true});
            skLineSegment(sketch, "E81.4.0.12", {"start": v(27.5, 39) * mm, "end": v(27.5, 45.13) * mm, "construction": true});
            skPoint(sketch, "E81.5.0.0", {"position": v(45.5, 59.5) * mm});
            skArc(sketch, "E81.5.0.1", {"start": v(47.3, 62.06) * mm, "mid": v(49.38, 62.43) * mm, "end": v(49.01, 64.52) * mm});
            skArc(sketch, "E81.5.0.2", {"start": v(41.99, 64.52) * mm, "mid": v(41.62, 62.43) * mm, "end": v(43.7, 62.06) * mm});
            skLineSegment(sketch, "E81.5.0.3", {"start": v(48.15, 63.29) * mm, "end": v(47.3, 62.06) * mm});
            skLineSegment(sketch, "E81.5.0.4", {"start": v(45.5, 59.5) * mm, "end": v(47.3, 62.06) * mm, "construction": true});
            skArc(sketch, "E81.5.0.5", {"start": v(49.01, 64.52) * mm, "mid": v(45.5, 65.63) * mm, "end": v(41.99, 64.52) * mm});
            skCircle(sketch, "E81.5.0.6", {"center": v(45.5, 59.5) * mm, "radius": 1.7 * mm});
            skArc(sketch, "E81.5.0.7", {"start": v(47.3, 62.06) * mm, "mid": v(45.5, 62.63) * mm, "end": v(43.7, 62.06) * mm});
            skLineSegment(sketch, "E81.5.0.8", {"start": v(45.5, 56.5) * mm, "end": v(45.5, 59.5) * mm, "construction": true});
            skLineSegment(sketch, "E81.5.0.9", {"start": v(45.5, 56.5) * mm, "end": v(52, 56.5) * mm});
            skLineSegment(sketch, "E81.5.0.10", {"start": v(43.7, 62.06) * mm, "end": v(42.85, 63.29) * mm});
            skLineSegment(sketch, "E81.5.0.11", {"start": v(45.5, 59.5) * mm, "end": v(43.7, 62.06) * mm, "construction": true});
            skLineSegment(sketch, "E81.5.0.12", {"start": v(45.5, 59.5) * mm, "end": v(45.5, 65.63) * mm, "construction": true});
            skLineSegment(sketch, "E81.direction1", {"start": v(-44.5, -43) * mm, "end": v(-26.5, -22.5) * mm, "construction": true});
            skSolve(sketch);
        }
        {
            var Q0;
            Q0 = qSketchRegion(id + "F10", true);
            extrude(context, id + "F11", {"entities" : qUnion([Q0]), "operationType" : NewBodyOperationType.REMOVE, "endBound" : BoundingType.THROUGH_ALL, "oppositeDirection" : true, "depth" : 25 * mm});
        }
        {
            var Q0;
            {var subQ0=sQuery(id+"F2.wireOp",EDGE,"E52.bottom");Q0=makeQuery(id+"F2.imprint","IMPRINT",FACE,{"disambiguationData":[TD([[makeQuery(id+"F2.imprint","IMPRINT",EDGE,{"derivedFrom":subQ0}),-1.0]])]});}
            var sketch = newSketch(context, id + "F12", { "sketchPlane" : qUnion([Q0])});
            skLineSegment(sketch, "E82.0", {"start": v(70, 78.8) * mm, "end": v(-72, 78.8) * mm});
            skLineSegment(sketch, "E83.0", {"start": v(70, 76.2) * mm, "end": v(-72, 76.2) * mm});
            skLineSegment(sketch, "E84", {"start": v(70, 76.2) * mm, "end": v(71.41, 74.79) * mm});
            skLineSegment(sketch, "E85", {"start": v(71.41, 74.79) * mm, "end": v(75.41, 74.79) * mm});
            skLineSegment(sketch, "E86", {"start": v(75.41, 74.79) * mm, "end": v(75.41, 78.8) * mm});
            skLineSegment(sketch, "E87", {"start": v(75.41, 78.8) * mm, "end": v(70, 78.8) * mm});
            skLineSegment(sketch, "E88", {"start": v(-72, 76.2) * mm, "end": v(-72, 78.8) * mm});
            skSolve(sketch);
        }
        {
            var Q0;
            Q0=makeQuery(id+"F12.imprint","IMPRINT",FACE,{"disambiguationData":[TD([[makeQuery(id+"F12.imprint","IMPRINT",EDGE,{"derivedFrom":sQuery(id+"F12.wireOp",EDGE,"E82.0")}),1.0]])]});
            var Q1;
            Q1=makeQuery(id+"F3.opExtrude","CAP_FACE",FACE,{"disambiguationData":[OSD([sQuery(id+"F0.wireOp",EDGE,"E0.left"),sQuery(id+"F0.wireOp",EDGE,"E0.right"),sQuery(id+"F2.wireOp",EDGE,"E2.1.0.0"),sQuery(id+"F2.wireOp",EDGE,"E2.3.0.0"),sQuery(id+"F2.wireOp",EDGE,"E2.5.0.0"),sQuery(id+"F2.wireOp",EDGE,"E2.7.0.0"),sQuery(id+"F2.wireOp",EDGE,"E2.9.0.0"),sQuery(id+"F2.wireOp",EDGE,"E2.11.0.0"),sQuery(id+"F2.wireOp",EDGE,"E4"),sQuery(id+"F2.wireOp",EDGE,"E6"),sQuery(id+"F2.wireOp",EDGE,"E7"),sQuery(id+"F2.wireOp",EDGE,"E9"),sQuery(id+"F2.wireOp",EDGE,"E10"),sQuery(id+"F2.wireOp",EDGE,"E12"),sQuery(id+"F2.wireOp",EDGE,"E13"),sQuery(id+"F2.wireOp",EDGE,"E15"),sQuery(id+"F2.wireOp",EDGE,"E16"),sQuery(id+"F2.wireOp",EDGE,"E18"),sQuery(id+"F2.wireOp",EDGE,"E19"),sQuery(id+"F2.wireOp",EDGE,"E21"),sQuery(id+"F2.wireOp",EDGE,"E22"),sQuery(id+"F2.wireOp",EDGE,"E23.trimOffspring"),sQuery(id+"F2.wireOp",EDGE,"E24.1.0.0"),sQuery(id+"F2.wireOp",EDGE,"E24.2.0.0"),sQuery(id+"F2.wireOp",EDGE,"E24.3.0.0"),sQuery(id+"F2.wireOp",EDGE,"E24.4.0.0"),sQuery(id+"F2.wireOp",EDGE,"E24.5.0.0"),sQuery(id+"F2.wireOp",EDGE,"E26.trimOffspring"),sQuery(id+"F2.wireOp",EDGE,"E27.trimOffspring"),sQuery(id+"F2.wireOp",EDGE,"E28.trimOffspring"),sQuery(id+"F2.wireOp",EDGE,"E29.trimOffspring"),sQuery(id+"F2.wireOp",EDGE,"E30.trimOffspring"),sQuery(id+"F2.wireOp",EDGE,"E31.bottom"),sQuery(id+"F2.wireOp",EDGE,"E31.top"),sQuery(id+"F2.wireOp",EDGE,"E31.left"),sQuery(id+"F2.wireOp",EDGE,"E31.right"),sQuery(id+"F2.wireOp",EDGE,"E32.1.0.0"),sQuery(id+"F2.wireOp",EDGE,"E32.1.0.1"),sQuery(id+"F2.wireOp",EDGE,"E32.1.0.2"),sQuery(id+"F2.wireOp",EDGE,"E32.1.0.3"),sQuery(id+"F2.wireOp",EDGE,"E32.2.0.0"),sQuery(id+"F2.wireOp",EDGE,"E32.2.0.1"),sQuery(id+"F2.wireOp",EDGE,"E32.2.0.2"),sQuery(id+"F2.wireOp",EDGE,"E32.2.0.3"),sQuery(id+"F2.wireOp",EDGE,"E32.3.0.0"),sQuery(id+"F2.wireOp",EDGE,"E32.3.0.1"),sQuery(id+"F2.wireOp",EDGE,"E32.3.0.2"),sQuery(id+"F2.wireOp",EDGE,"E32.3.0.3"),sQuery(id+"F2.wireOp",EDGE,"E32.4.0.0"),sQuery(id+"F2.wireOp",EDGE,"E32.4.0.1"),sQuery(id+"F2.wireOp",EDGE,"E32.4.0.2"),sQuery(id+"F2.wireOp",EDGE,"E32.4.0.3"),sQuery(id+"F2.wireOp",EDGE,"E33"),sQuery(id+"F2.wireOp",EDGE,"E34"),sQuery(id+"F2.wireOp",EDGE,"E35"),sQuery(id+"F2.wireOp",EDGE,"E36"),sQuery(id+"F2.wireOp",EDGE,"E37"),sQuery(id+"F2.wireOp",EDGE,"E38"),sQuery(id+"F2.wireOp",EDGE,"E39"),sQuery(id+"F2.wireOp",EDGE,"E41"),sQuery(id+"F2.wireOp",EDGE,"E42"),sQuery(id+"F2.wireOp",EDGE,"E43"),sQuery(id+"F2.wireOp",EDGE,"E44"),sQuery(id+"F2.wireOp",EDGE,"E46"),sQuery(id+"F2.wireOp",EDGE,"E47"),sQuery(id+"F2.wireOp",EDGE,"E48.top"),sQuery(id+"F2.wireOp",EDGE,"E48.left"),sQuery(id+"F2.wireOp",EDGE,"E48.right"),sQuery(id+"F2.wireOp",EDGE,"E51.top"),sQuery(id+"F2.wireOp",EDGE,"E51.left"),sQuery(id+"F2.wireOp",EDGE,"E51.right")])],"isStart":false});
            extrude(context, id + "F13", {"entities" : qUnion([Q0]), "endBound" : BoundingType.UP_TO_SURFACE, "endBoundEntityFace" : qUnion([Q1]), "depth" : 25 * mm});
        }
        {
            var Q0;
            {var subQ0=sQuery(id+"F6.wireOp",EDGE,"E60");var subQ1=makeQuery(id+"F6.imprint","INTERSECT",VERTEX,{"derivedFrom":[sQuery(id+"F6.wireOp",EDGE,"E59.0.1"),subQ0]});Q0=makeQuery(id+"F6.imprint","IMPRINT",FACE,{"disambiguationData":[TD([[makeQuery(id+"F6.imprint","IMPRINT",EDGE,{"disambiguationData":[TD([[subQ1,-1.0]])],"derivedFrom":subQ0}),1.0]])]});}
            var Q1;
            Q1=makeQuery(id+"F6.imprint","IMPRINT",FACE,{"disambiguationData":[TD([[makeQuery(id+"F6.imprint","IMPRINT",EDGE,{"derivedFrom":sQuery(id+"F6.wireOp",EDGE,"E61.1.0.0")}),1.0]])]});
            var Q2;
            Q2=makeQuery(id+"F6.imprint","IMPRINT",FACE,{"disambiguationData":[TD([[makeQuery(id+"F6.imprint","IMPRINT",EDGE,{"derivedFrom":sQuery(id+"F6.wireOp",EDGE,"E61.2.0.0")}),1.0]])]});
            var Q3;
            Q3=makeQuery(id+"F6.imprint","IMPRINT",FACE,{"disambiguationData":[TD([[makeQuery(id+"F6.imprint","IMPRINT",EDGE,{"derivedFrom":sQuery(id+"F6.wireOp",EDGE,"E61.5.0.0")}),1.0]])]});
            var Q4;
            Q4=makeQuery(id+"F6.imprint","IMPRINT",FACE,{"disambiguationData":[TD([[makeQuery(id+"F6.imprint","IMPRINT",EDGE,{"derivedFrom":sQuery(id+"F6.wireOp",EDGE,"E61.4.0.0")}),1.0]])]});
            var Q5;
            Q5=makeQuery(id+"F6.imprint","IMPRINT",FACE,{"disambiguationData":[TD([[makeQuery(id+"F6.imprint","IMPRINT",EDGE,{"derivedFrom":sQuery(id+"F6.wireOp",EDGE,"E61.3.0.0")}),1.0]])]});
            var Q6;
            Q6=makeQuery(id+"F13.opExtrude","SWEPT_FACE",FACE,{"disambiguationData":[OSD([sQuery(id+"F12.wireOp",EDGE,"E82.0"),sQuery(id+"F12.wireOp",EDGE,"E87")])]});
            extrude(context, id + "F14", {"entities" : qUnion([Q0, Q1, Q2, Q3, Q4, Q5]), "operationType" : NewBodyOperationType.REMOVE, "endBound" : BoundingType.UP_TO_SURFACE, "endBoundEntityFace" : qUnion([Q6]), "depth" : 25 * mm});
        }
        {
            var Q0;
            {var subQ0=sQuery(id+"F8.wireOp",EDGE,"E63");var subQ1=makeQuery(id+"F8.imprint","INTERSECT",VERTEX,{"derivedFrom":[sQuery(id+"F8.wireOp",EDGE,"E62.0.1"),subQ0]});Q0=makeQuery(id+"F8.imprint","IMPRINT",FACE,{"disambiguationData":[TD([[makeQuery(id+"F8.imprint","IMPRINT",EDGE,{"disambiguationData":[TD([[subQ1,1.0]])],"derivedFrom":subQ0}),1.0]])]});}
            var Q1;
            Q1=makeQuery(id+"F8.imprint","IMPRINT",FACE,{"disambiguationData":[TD([[makeQuery(id+"F8.imprint","IMPRINT",EDGE,{"derivedFrom":sQuery(id+"F8.wireOp",EDGE,"E64.1.0.0")}),1.0]])]});
            var Q2;
            Q2=makeQuery(id+"F8.imprint","IMPRINT",FACE,{"disambiguationData":[TD([[makeQuery(id+"F8.imprint","IMPRINT",EDGE,{"derivedFrom":sQuery(id+"F8.wireOp",EDGE,"E64.2.0.0")}),1.0]])]});
            var Q3;
            Q3=makeQuery(id+"F8.imprint","IMPRINT",FACE,{"disambiguationData":[TD([[makeQuery(id+"F8.imprint","IMPRINT",EDGE,{"derivedFrom":sQuery(id+"F8.wireOp",EDGE,"E64.3.0.0")}),1.0]])]});
            var Q4;
            Q4=makeQuery(id+"F8.imprint","IMPRINT",FACE,{"disambiguationData":[TD([[makeQuery(id+"F8.imprint","IMPRINT",EDGE,{"derivedFrom":sQuery(id+"F8.wireOp",EDGE,"E64.4.0.0")}),1.0]])]});
            var Q5;
            Q5=makeQuery(id+"F8.imprint","IMPRINT",FACE,{"disambiguationData":[TD([[makeQuery(id+"F8.imprint","IMPRINT",EDGE,{"derivedFrom":sQuery(id+"F8.wireOp",EDGE,"E64.5.0.0")}),1.0]])]});
            var Q6;
            Q6=makeQuery(id+"F8.imprint","IMPRINT",FACE,{"disambiguationData":[TD([[makeQuery(id+"F8.imprint","IMPRINT",EDGE,{"derivedFrom":sQuery(id+"F8.wireOp",EDGE,"E65.1.0.0")}),1.0]])]});
            var Q7;
            Q7=makeQuery(id+"F3.opExtrude","SWEPT_FACE",FACE,{"disambiguationData":[OSD([sQuery(id+"F2.wireOp",EDGE,"E57.top")])]});
            extrude(context, id + "F15", {"entities" : qUnion([Q0, Q1, Q2, Q3, Q4, Q5, Q6]), "operationType" : NewBodyOperationType.REMOVE, "endBound" : BoundingType.UP_TO_SURFACE, "endBoundEntityFace" : qUnion([Q7]), "depth" : 25 * mm});
        }
        {
            var Q0;
            Q0=makeQuery(id+"F1.opExtrude","CAP_FACE",FACE,{"disambiguationData":[OSD([sQuery(id+"F0.wireOp",EDGE,"E0.bottom"),sQuery(id+"F0.wireOp",EDGE,"E0.top"),sQuery(id+"F0.wireOp",EDGE,"E0.left"),sQuery(id+"F0.wireOp",EDGE,"E0.right")])],"isStart":false});
            var sketch = newSketch(context, id + "F16", { "sketchPlane" : qUnion([Q0])});
            skLineSegment(sketch, "E89.bottom", {"start": v(70, -70.5) * mm, "end": v(-70, -70.5) * mm});
            skLineSegment(sketch, "E89.top", {"start": v(70, -73.5) * mm, "end": v(-70, -73.5) * mm});
            skLineSegment(sketch, "E89.left", {"start": v(70, -70.5) * mm, "end": v(70, -73.5) * mm});
            skLineSegment(sketch, "E89.right", {"start": v(-70, -70.5) * mm, "end": v(-70, -73.5) * mm});
            skCircle(sketch, "E90.0", {"center": v(44.5, -43) * mm, "radius": 1.7 * mm});
            skCircle(sketch, "E91.0", {"center": v(-45.5, 59.5) * mm, "radius": 1.7 * mm});
            skLineSegment(sketch, "E92", {"start": v(-45.5, 59.5) * mm, "end": v(44.5, -43) * mm, "construction": true});
            skLineSegment(sketch, "E93", {"start": v(56.65, -70.5) * mm, "end": v(29.76, -39.88) * mm});
            skPoint(sketch, "E94", {"position": v(32.5, -43) * mm});
            skLineSegment(sketch, "E95", {"start": v(-45.5, 65.63) * mm, "end": v(-70, 65.63) * mm, "construction": true});
            skLineSegment(sketch, "E96.0", {"start": v(50.02, -67.5) * mm, "end": v(-62.4, 60.53) * mm});
            skLineSegment(sketch, "E97.0", {"start": v(75, 105) * mm, "end": v(-75, 105) * mm});
            skLineSegment(sketch, "E97.1", {"start": v(75, -105) * mm, "end": v(75, 105) * mm});
            skLineSegment(sketch, "E97.2", {"start": v(-75, -105) * mm, "end": v(75, -105) * mm});
            skLineSegment(sketch, "E97.3", {"start": v(-75, 105) * mm, "end": v(-75, -105) * mm});
            skLineSegment(sketch, "E98", {"start": v(38.62, -39.88) * mm, "end": v(29.76, -39.88) * mm});
            skPoint(sketch, "E98.startSnap0", {"position": v(44.5, -39.88) * mm});
            skLineSegment(sketch, "E99", {"start": v(38.62, -36.88) * mm, "end": v(27.12, -36.88) * mm, "construction": true});
            skPoint(sketch, "E99.startSnap0", {"position": v(44.5, -36.88) * mm});
            skLineSegment(sketch, "E100", {"start": v(38.62, -39.88) * mm, "end": v(38.62, -36.88) * mm});
            skLineSegment(sketch, "E101.trimOffspring", {"start": v(27.12, -36.88) * mm, "end": v(11.76, -19.38) * mm});
            skLineSegment(sketch, "E102", {"start": v(38.62, -36.88) * mm, "end": v(21.72, -30.72) * mm});
            skLineSegment(sketch, "E103.1.0.0", {"start": v(20.62, -19.38) * mm, "end": v(11.76, -19.38) * mm});
            skLineSegment(sketch, "E103.1.0.1", {"start": v(20.62, -19.38) * mm, "end": v(20.62, -16.38) * mm});
            skLineSegment(sketch, "E103.1.0.2", {"start": v(20.62, -16.38) * mm, "end": v(3.72, -10.22) * mm});
            skPoint(sketch, "E103.1.0.3", {"position": v(26.5, -19.38) * mm});
            skLineSegment(sketch, "E103.2.0.0", {"start": v(2.62, 1.13) * mm, "end": v(-6.24, 1.13) * mm});
            skLineSegment(sketch, "E103.2.0.1", {"start": v(2.62, 1.13) * mm, "end": v(2.62, 4.13) * mm});
            skLineSegment(sketch, "E103.2.0.2", {"start": v(2.62, 4.13) * mm, "end": v(-14.28, 10.28) * mm});
            skPoint(sketch, "E103.2.0.3", {"position": v(8.5, 1.13) * mm});
            skLineSegment(sketch, "E103.3.0.0", {"start": v(-15.38, 21.63) * mm, "end": v(-24.24, 21.63) * mm});
            skLineSegment(sketch, "E103.3.0.1", {"start": v(-15.38, 21.63) * mm, "end": v(-15.38, 24.63) * mm});
            skLineSegment(sketch, "E103.3.0.2", {"start": v(-15.38, 24.63) * mm, "end": v(-32.28, 30.78) * mm});
            skPoint(sketch, "E103.3.0.3", {"position": v(-9.5, 21.63) * mm});
            skLineSegment(sketch, "E103.4.0.0", {"start": v(-33.38, 42.13) * mm, "end": v(-42.24, 42.13) * mm});
            skLineSegment(sketch, "E103.4.0.1", {"start": v(-33.38, 42.13) * mm, "end": v(-33.38, 45.13) * mm});
            skLineSegment(sketch, "E103.4.0.2", {"start": v(-33.38, 45.13) * mm, "end": v(-50.28, 51.28) * mm});
            skPoint(sketch, "E103.4.0.3", {"position": v(-27.5, 42.13) * mm});
            skLineSegment(sketch, "E103.5.0.0", {"start": v(-51.38, 62.63) * mm, "end": v(-60.24, 62.63) * mm});
            skLineSegment(sketch, "E103.5.0.1", {"start": v(-51.38, 62.63) * mm, "end": v(-51.38, 65.63) * mm});
            skLineSegment(sketch, "E103.5.0.2", {"start": v(-51.38, 65.63) * mm, "end": v(-65.06, 70.6) * mm});
            skPoint(sketch, "E103.5.0.3", {"position": v(-45.5, 62.63) * mm});
            skLineSegment(sketch, "E103.direction1", {"start": v(29.76, -39.88) * mm, "end": v(11.76, -19.37) * mm, "construction": true});
            skLineSegment(sketch, "E104.trimOffspring", {"start": v(3.72, -10.22) * mm, "end": v(-6.24, 1.13) * mm});
            skLineSegment(sketch, "E105.trimOffspring", {"start": v(-14.28, 10.28) * mm, "end": v(-24.24, 21.63) * mm});
            skLineSegment(sketch, "E106.trimOffspring", {"start": v(-32.28, 30.78) * mm, "end": v(-42.24, 42.13) * mm});
            skLineSegment(sketch, "E107.trimOffspring", {"start": v(-50.28, 51.28) * mm, "end": v(-60.24, 62.63) * mm});
            skLineSegment(sketch, "E108", {"start": v(-66.87, 65.63) * mm, "end": v(-65.06, 70.6) * mm});
            skPoint(sketch, "E109.orphan", {"position": v(-68.28, 71.78) * mm});
            skPoint(sketch, "E110.0", {"position": v(-70, -70.5) * mm});
            skLineSegment(sketch, "E111", {"start": v(-66.87, 65.63) * mm, "end": v(-30.4, -70.5) * mm});
            skLineSegment(sketch, "E112", {"start": v(52.65, -70.5) * mm, "end": v(-30.4, -70.5) * mm});
            skLineSegment(sketch, "E113", {"start": v(50.02, -67.5) * mm, "end": v(-28.1, -67.5) * mm});
            skLineSegment(sketch, "E114", {"start": v(-28.1, -67.5) * mm, "end": v(-62.4, 60.53) * mm});
            skSolve(sketch);
        }
        {
            var Q0;
            {var subQ1=sQuery(id+"F16.wireOp",EDGE,"E93");Q0=makeQuery(id+"F16.imprint","IMPRINT",FACE,{"disambiguationData":[TD([[makeQuery(id+"F16.imprint","IMPRINT",EDGE,{"derivedFrom":subQ1}),1.0]])]});}
            extrude(context, id + "F17", {"entities" : qUnion([Q0]), "depth" : 3 * mm});
        }
        {
            var Q0;
            Q0=makeQuery(id+"F16.imprint","IMPRINT",FACE,{"disambiguationData":[TD([[makeQuery(id+"F16.imprint","IMPRINT",EDGE,{"derivedFrom":sQuery(id+"F16.wireOp",EDGE,"E89.top")}),-1.0]])]});
            extrude(context, id + "F18", {"entities" : qUnion([Q0]), "operationType" : NewBodyOperationType.ADD, "depth" : 3 * mm});
        }
        {
            var Q0;
            Q0=makeQuery(id+"F3.opExtrude","CAP_FACE",FACE,{"disambiguationData":[OSD([sQuery(id+"F0.wireOp",EDGE,"E0.left"),sQuery(id+"F0.wireOp",EDGE,"E0.right"),sQuery(id+"F2.wireOp",EDGE,"E2.1.0.0"),sQuery(id+"F2.wireOp",EDGE,"E2.3.0.0"),sQuery(id+"F2.wireOp",EDGE,"E2.5.0.0"),sQuery(id+"F2.wireOp",EDGE,"E2.7.0.0"),sQuery(id+"F2.wireOp",EDGE,"E2.9.0.0"),sQuery(id+"F2.wireOp",EDGE,"E2.11.0.0"),sQuery(id+"F2.wireOp",EDGE,"E4"),sQuery(id+"F2.wireOp",EDGE,"E6"),sQuery(id+"F2.wireOp",EDGE,"E7"),sQuery(id+"F2.wireOp",EDGE,"E9"),sQuery(id+"F2.wireOp",EDGE,"E10"),sQuery(id+"F2.wireOp",EDGE,"E12"),sQuery(id+"F2.wireOp",EDGE,"E13"),sQuery(id+"F2.wireOp",EDGE,"E15"),sQuery(id+"F2.wireOp",EDGE,"E16"),sQuery(id+"F2.wireOp",EDGE,"E18"),sQuery(id+"F2.wireOp",EDGE,"E19"),sQuery(id+"F2.wireOp",EDGE,"E21"),sQuery(id+"F2.wireOp",EDGE,"E22"),sQuery(id+"F2.wireOp",EDGE,"E23.trimOffspring"),sQuery(id+"F2.wireOp",EDGE,"E24.1.0.0"),sQuery(id+"F2.wireOp",EDGE,"E24.2.0.0"),sQuery(id+"F2.wireOp",EDGE,"E24.3.0.0"),sQuery(id+"F2.wireOp",EDGE,"E24.4.0.0"),sQuery(id+"F2.wireOp",EDGE,"E24.5.0.0"),sQuery(id+"F2.wireOp",EDGE,"E26.trimOffspring"),sQuery(id+"F2.wireOp",EDGE,"E27.trimOffspring"),sQuery(id+"F2.wireOp",EDGE,"E28.trimOffspring"),sQuery(id+"F2.wireOp",EDGE,"E29.trimOffspring"),sQuery(id+"F2.wireOp",EDGE,"E30.trimOffspring"),sQuery(id+"F2.wireOp",EDGE,"E31.bottom"),sQuery(id+"F2.wireOp",EDGE,"E31.top"),sQuery(id+"F2.wireOp",EDGE,"E31.left"),sQuery(id+"F2.wireOp",EDGE,"E31.right"),sQuery(id+"F2.wireOp",EDGE,"E32.1.0.0"),sQuery(id+"F2.wireOp",EDGE,"E32.1.0.1"),sQuery(id+"F2.wireOp",EDGE,"E32.1.0.2"),sQuery(id+"F2.wireOp",EDGE,"E32.1.0.3"),sQuery(id+"F2.wireOp",EDGE,"E32.2.0.0"),sQuery(id+"F2.wireOp",EDGE,"E32.2.0.1"),sQuery(id+"F2.wireOp",EDGE,"E32.2.0.2"),sQuery(id+"F2.wireOp",EDGE,"E32.2.0.3"),sQuery(id+"F2.wireOp",EDGE,"E32.3.0.0"),sQuery(id+"F2.wireOp",EDGE,"E32.3.0.1"),sQuery(id+"F2.wireOp",EDGE,"E32.3.0.2"),sQuery(id+"F2.wireOp",EDGE,"E32.3.0.3"),sQuery(id+"F2.wireOp",EDGE,"E32.4.0.0"),sQuery(id+"F2.wireOp",EDGE,"E32.4.0.1"),sQuery(id+"F2.wireOp",EDGE,"E32.4.0.2"),sQuery(id+"F2.wireOp",EDGE,"E32.4.0.3"),sQuery(id+"F2.wireOp",EDGE,"E33"),sQuery(id+"F2.wireOp",EDGE,"E34"),sQuery(id+"F2.wireOp",EDGE,"E35"),sQuery(id+"F2.wireOp",EDGE,"E36"),sQuery(id+"F2.wireOp",EDGE,"E37"),sQuery(id+"F2.wireOp",EDGE,"E38"),sQuery(id+"F2.wireOp",EDGE,"E39"),sQuery(id+"F2.wireOp",EDGE,"E41"),sQuery(id+"F2.wireOp",EDGE,"E42"),sQuery(id+"F2.wireOp",EDGE,"E43"),sQuery(id+"F2.wireOp",EDGE,"E44"),sQuery(id+"F2.wireOp",EDGE,"E46"),sQuery(id+"F2.wireOp",EDGE,"E47"),sQuery(id+"F2.wireOp",EDGE,"E48.top"),sQuery(id+"F2.wireOp",EDGE,"E48.left"),sQuery(id+"F2.wireOp",EDGE,"E48.right"),sQuery(id+"F2.wireOp",EDGE,"E51.top"),sQuery(id+"F2.wireOp",EDGE,"E51.left"),sQuery(id+"F2.wireOp",EDGE,"E51.right")])],"isStart":false});
            var sketch = newSketch(context, id + "F19", { "sketchPlane" : qUnion([Q0])});
            skLineSegment(sketch, "E115.bottom", {"start": v(-40, -9) * mm, "end": v(16, -9) * mm});
            skLineSegment(sketch, "E115.top", {"start": v(-40, 15.5) * mm, "end": v(16, 15.5) * mm});
            skLineSegment(sketch, "E115.left", {"start": v(-40, -9) * mm, "end": v(-40, 15.5) * mm});
            skLineSegment(sketch, "E115.right", {"start": v(16, -9) * mm, "end": v(16, 15.5) * mm});
            skSolve(sketch);
        }
        {
            var Q0;
            Q0=makeQuery(id+"F3.boolean.opBoolean","SPLIT",FACE,{"disambiguationData":[TD([makeQuery(id+"F3.opExtrude","SWEPT_FACE",FACE,{"disambiguationData":[OSD([sQuery(id+"F2.wireOp",EDGE,"E2.7.0.0")])]})])],"derivedFrom":makeQuery(id+"F1.opExtrude","CAP_FACE",FACE,{"disambiguationData":[OSD([sQuery(id+"F0.wireOp",EDGE,"E0.bottom"),sQuery(id+"F0.wireOp",EDGE,"E0.top"),sQuery(id+"F0.wireOp",EDGE,"E0.left"),sQuery(id+"F0.wireOp",EDGE,"E0.right")])],"isStart":true})});
            var sketch = newSketch(context, id + "F20", { "sketchPlane" : qUnion([Q0])});
            skArc(sketch, "E116", {"start": v(-21.33, 0.2) * mm, "mid": v(-21.44, -0.6) * mm, "end": v(-21.5, -1.41) * mm});
            skLineSegment(sketch, "E117", {"start": v(-8.5, 4.7) * mm, "end": v(-14.93, 0.2) * mm});
            skLineSegment(sketch, "E118", {"start": v(-14.93, 0.2) * mm, "end": v(-21.33, 0.2) * mm});
            skLineSegment(sketch, "E119.MirrorCS", {"start": v(-8.5, 4.7) * mm, "end": v(-2.07, 0.2) * mm});
            skLineSegment(sketch, "E120.MirrorCS", {"start": v(-2.07, 0.2) * mm, "end": v(4.33, 0.2) * mm});
            skArc(sketch, "E121.trimOffspring", {"start": v(4.5, -1.41) * mm, "mid": v(4.44, -0.6) * mm, "end": v(4.33, 0.2) * mm});
            skCircle(sketch, "E122", {"center": v(-8.5, -2) * mm, "radius": 1.5 * mm});
            skLineSegment(sketch, "E123", {"start": v(-8.5, -2) * mm, "end": v(-8.5, 7.38) * mm, "construction": true});
            skArc(sketch, "E124", {"start": v(-9.22, -4.7) * mm, "mid": v(-8.5, -4.8) * mm, "end": v(-7.78, -4.7) * mm});
            skLineSegment(sketch, "E125", {"start": v(-7.78, -4.7) * mm, "end": v(4.5, -1.41) * mm});
            skLineSegment(sketch, "E126.0", {"start": v(-2, -5) * mm, "end": v(-31, -5) * mm});
            skPoint(sketch, "E127.orphan", {"position": v(4.5, -1.6) * mm});
            skLineSegment(sketch, "E128.MirrorCS", {"start": v(-9.22, -4.7) * mm, "end": v(-21.5, -1.41) * mm});
            skPoint(sketch, "E129.orphan", {"position": v(-21.5, -1.22) * mm});
            skPoint(sketch, "E130", {"position": v(-8.5, -4.87) * mm});
            skSolve(sketch);
        }
        {
            var Q0;
            Q0=makeQuery(id+"F20.imprint","IMPRINT",FACE,{"disambiguationData":[TD([[makeQuery(id+"F20.imprint","IMPRINT",EDGE,{"derivedFrom":sQuery(id+"F20.wireOp",EDGE,"E116")}),1.0]])]});
            var Q1;
            {var subQ0=makeQuery(id+"F11.boolean.opBoolean","COPY",EDGE,{"derivedFrom":makeQuery(id+"F11.opExtrude","CAP_EDGE",EDGE,{"disambiguationData":[OSD([sQuery(id+"F10.wireOp",EDGE,"E81.2.0.7")])],"isStart":true})});Q1=makeQuery(id+"F20.imprint","IMPRINT",FACE,{"disambiguationData":[TD([[makeQuery(id+"F20.imprint","IMPRINT",EDGE,{"derivedFrom":subQ0}),-1.0]])]});}
            var Q2;
            Q2=makeQuery(id+"F20.imprint","IMPRINT",FACE,{"disambiguationData":[TD([[makeQuery(id+"F20.imprint","IMPRINT",EDGE,{"derivedFrom":sQuery(id+"F20.wireOp",EDGE,"E122")}),-1.0]])]});
            var Q3;
            {var subQ0=sQuery(id+"F20.wireOp",EDGE,"E119.MirrorCS");var subQ1=sQuery(id+"F20.wireOp",EDGE,"E117");var subQ2=makeQuery(id+"F20.imprint","INTERSECT",VERTEX,{"derivedFrom":[subQ1,subQ0]});Q3=makeQuery(id+"F20.imprint","IMPRINT",FACE,{"disambiguationData":[TD([[makeQuery(id+"F20.imprint","IMPRINT",EDGE,{"disambiguationData":[TD([[subQ2,-1.0]])],"derivedFrom":subQ1}),1.0]])]});}
            var Q4;
            {var subQ3=sQuery(id+"F20.wireOp",EDGE,"fa6f81bb-2618-4b47-be0c-2e972fa51a74.trimOffspring");Q4=makeQuery(id+"F20.imprint","IMPRINT",FACE,{"disambiguationData":[TD([[makeQuery(id+"F20.imprint","IMPRINT",EDGE,{"derivedFrom":subQ3}),1.0]])]});}
            var Q5;
            {var subQ0=sQuery(id+"F2.wireOp",EDGE,"E32.3.0.2");var subQ1=sQuery(id+"F2.wireOp",EDGE,"E32.3.0.0");var subQ2=sQuery(id+"F2.wireOp",EDGE,"E32.2.0.2");var subQ3=sQuery(id+"F2.wireOp",EDGE,"E32.3.0.1");var subQ4=sQuery(id+"F2.wireOp",EDGE,"E7");var subQ5=sQuery(id+"F2.wireOp",EDGE,"E37");var subQ6=sQuery(id+"F2.wireOp",EDGE,"E32.3.0.3");var subQ7=sQuery(id+"F2.wireOp",EDGE,"E43");Q5=makeQuery(id+"FEBG0xOLVOlM8Ji_3.boolean.opBoolean","SPLIT",FACE,{"disambiguationData":[TD([makeQuery(id+"F3.opExtrude","SWEPT_FACE",FACE,{"disambiguationData":[OSD([subQ0])]})])],"derivedFrom":makeQuery(id+"F3.opExtrude","CAP_FACE",FACE,{"disambiguationData":[OSD([sQuery(id+"F0.wireOp",EDGE,"E0.left"),sQuery(id+"F0.wireOp",EDGE,"E0.right"),sQuery(id+"F2.wireOp",EDGE,"E2.1.0.0"),sQuery(id+"F2.wireOp",EDGE,"E2.3.0.0"),sQuery(id+"F2.wireOp",EDGE,"E2.5.0.0"),sQuery(id+"F2.wireOp",EDGE,"E2.7.0.0"),sQuery(id+"F2.wireOp",EDGE,"E2.9.0.0"),sQuery(id+"F2.wireOp",EDGE,"E2.11.0.0"),sQuery(id+"F2.wireOp",EDGE,"E4"),sQuery(id+"F2.wireOp",EDGE,"E6"),subQ4,sQuery(id+"F2.wireOp",EDGE,"E9"),sQuery(id+"F2.wireOp",EDGE,"E10"),sQuery(id+"F2.wireOp",EDGE,"E12"),sQuery(id+"F2.wireOp",EDGE,"E13"),sQuery(id+"F2.wireOp",EDGE,"E15"),sQuery(id+"F2.wireOp",EDGE,"E16"),sQuery(id+"F2.wireOp",EDGE,"E18"),sQuery(id+"F2.wireOp",EDGE,"E19"),sQuery(id+"F2.wireOp",EDGE,"E21"),sQuery(id+"F2.wireOp",EDGE,"E22"),sQuery(id+"F2.wireOp",EDGE,"E23.trimOffspring"),sQuery(id+"F2.wireOp",EDGE,"E24.1.0.0"),sQuery(id+"F2.wireOp",EDGE,"E24.2.0.0"),sQuery(id+"F2.wireOp",EDGE,"E24.3.0.0"),sQuery(id+"F2.wireOp",EDGE,"E24.4.0.0"),sQuery(id+"F2.wireOp",EDGE,"E24.5.0.0"),sQuery(id+"F2.wireOp",EDGE,"E26.trimOffspring"),sQuery(id+"F2.wireOp",EDGE,"E27.trimOffspring"),sQuery(id+"F2.wireOp",EDGE,"E28.trimOffspring"),sQuery(id+"F2.wireOp",EDGE,"E29.trimOffspring"),sQuery(id+"F2.wireOp",EDGE,"E30.trimOffspring"),sQuery(id+"F2.wireOp",EDGE,"E31.bottom"),sQuery(id+"F2.wireOp",EDGE,"E31.top"),sQuery(id+"F2.wireOp",EDGE,"E31.left"),sQuery(id+"F2.wireOp",EDGE,"E31.right"),sQuery(id+"F2.wireOp",EDGE,"E32.1.0.0"),sQuery(id+"F2.wireOp",EDGE,"E32.1.0.1"),sQuery(id+"F2.wireOp",EDGE,"E32.1.0.2"),sQuery(id+"F2.wireOp",EDGE,"E32.1.0.3"),sQuery(id+"F2.wireOp",EDGE,"E32.2.0.0"),sQuery(id+"F2.wireOp",EDGE,"E32.2.0.1"),subQ2,sQuery(id+"F2.wireOp",EDGE,"E32.2.0.3"),subQ1,subQ3,subQ0,subQ6,sQuery(id+"F2.wireOp",EDGE,"E32.4.0.0"),sQuery(id+"F2.wireOp",EDGE,"E32.4.0.1"),sQuery(id+"F2.wireOp",EDGE,"E32.4.0.2"),sQuery(id+"F2.wireOp",EDGE,"E32.4.0.3"),sQuery(id+"F2.wireOp",EDGE,"E33"),sQuery(id+"F2.wireOp",EDGE,"E34"),sQuery(id+"F2.wireOp",EDGE,"E35"),sQuery(id+"F2.wireOp",EDGE,"E36"),subQ5,sQuery(id+"F2.wireOp",EDGE,"E38"),sQuery(id+"F2.wireOp",EDGE,"E39"),sQuery(id+"F2.wireOp",EDGE,"E41"),sQuery(id+"F2.wireOp",EDGE,"E42"),subQ7,sQuery(id+"F2.wireOp",EDGE,"E44"),sQuery(id+"F2.wireOp",EDGE,"E46"),sQuery(id+"F2.wireOp",EDGE,"E47"),sQuery(id+"F2.wireOp",EDGE,"E48.top"),sQuery(id+"F2.wireOp",EDGE,"E48.left"),sQuery(id+"F2.wireOp",EDGE,"E48.right"),sQuery(id+"F2.wireOp",EDGE,"E51.top"),sQuery(id+"F2.wireOp",EDGE,"E51.left"),sQuery(id+"F2.wireOp",EDGE,"E51.right")])],"isStart":false})});}
            extrude(context, id + "F21", {"entities" : qUnion([Q0, Q1, Q2, Q3, Q4]), "endBound" : BoundingType.UP_TO_SURFACE, "endBoundEntityFace" : qUnion([Q5]), "depth" : 25 * mm});
        }
        {
            var Q0;
            Q0=makeQuery(id+"F21.opExtrude","CAP_FACE",FACE,{"disambiguationData":[OSD([sQuery(id+"F20.wireOp",EDGE,"E116"),sQuery(id+"F20.wireOp",EDGE,"E117"),sQuery(id+"F20.wireOp",EDGE,"E118"),sQuery(id+"F20.wireOp",EDGE,"E119.MirrorCS"),sQuery(id+"F20.wireOp",EDGE,"E120.MirrorCS"),sQuery(id+"F20.wireOp",EDGE,"E121.trimOffspring"),sQuery(id+"F20.wireOp",EDGE,"E122"),sQuery(id+"F20.wireOp",EDGE,"E124"),sQuery(id+"F20.wireOp",EDGE,"E125"),sQuery(id+"F20.wireOp",EDGE,"E128.MirrorCS")])],"isStart":false});
            var sketch = newSketch(context, id + "F22", { "sketchPlane" : qUnion([Q0])});
            skArc(sketch, "E131.1", {"start": v(-22.92, 2.2) * mm, "mid": v(-23.28, 0.67) * mm, "end": v(-23.47, -0.89) * mm});
            skLineSegment(sketch, "E131.2", {"start": v(-15.56, 2.2) * mm, "end": v(-22.92, 2.2) * mm});
            skLineSegment(sketch, "E131.3", {"start": v(-8.5, 7.14) * mm, "end": v(-15.56, 2.2) * mm});
            skLineSegment(sketch, "E131.4", {"start": v(-1.44, 2.2) * mm, "end": v(-8.5, 7.14) * mm});
            skArc(sketch, "E131.9", {"start": v(6.47, -0.89) * mm, "mid": v(6.28, 0.67) * mm, "end": v(5.92, 2.2) * mm});
            skLineSegment(sketch, "E131.10", {"start": v(5.92, 2.2) * mm, "end": v(-1.44, 2.2) * mm});
            skLineSegment(sketch, "E132.0", {"start": v(4.5, -1.41) * mm, "end": v(6.47, -0.89) * mm});
            skLineSegment(sketch, "E133.0", {"start": v(-9.22, -4.7) * mm, "end": v(-21.5, -1.41) * mm});
            skLineSegment(sketch, "E134.2", {"start": v(-9.22, -4.7) * mm, "end": v(-23.47, -0.89) * mm});
            skLineSegment(sketch, "E134.3", {"start": v(-14.93, 0.2) * mm, "end": v(-21.33, 0.2) * mm});
            skLineSegment(sketch, "E134.4", {"start": v(-8.5, 4.7) * mm, "end": v(-14.93, 0.2) * mm});
            skLineSegment(sketch, "E134.6", {"start": v(-8.5, 4.7) * mm, "end": v(-14.93, 0.2) * mm});
            skLineSegment(sketch, "E134.7", {"start": v(-14.93, 0.2) * mm, "end": v(-21.33, 0.2) * mm});
            skPoint(sketch, "E135.orphan", {"position": v(-7.78, -4.7) * mm});
            skLineSegment(sketch, "E136.0", {"start": v(-9.22, -4.7) * mm, "end": v(-9.22, -4.7) * mm});
            skLineSegment(sketch, "E137.0", {"start": v(-7.78, -4.7) * mm, "end": v(4.5, -1.41) * mm});
            skArc(sketch, "E138.0", {"start": v(-9.22, -4.7) * mm, "mid": v(-8.5, -4.8) * mm, "end": v(-7.78, -4.7) * mm});
            skSolve(sketch);
        }
        {
            var Q0;
            {var subQ3=sQuery(id+"F22.wireOp",EDGE,"E131.2");Q0=makeQuery(id+"F22.imprint","IMPRINT",FACE,{"disambiguationData":[TD([[makeQuery(id+"F22.imprint","IMPRINT",EDGE,{"derivedFrom":subQ3}),1.0]])]});}
            var Q1;
            Q1=makeQuery(id+"F22.imprint","IMPRINT",FACE,{"disambiguationData":[TD([[makeQuery(id+"F22.imprint","IMPRINT",EDGE,{"derivedFrom":sQuery(id+"F22.wireOp",EDGE,"E134.6")}),1.0]])]});
            var Q2;
            Q2=makeQuery(id+"F22.imprint","IMPRINT",FACE,{"disambiguationData":[TD([[makeQuery(id+"F22.imprint","IMPRINT",EDGE,{"derivedFrom":makeQuery(id+"F21.opExtrude","CAP_EDGE",EDGE,{"disambiguationData":[OSD([sQuery(id+"F20.wireOp",EDGE,"E122")])],"isStart":false})}),1.0]])]});
            extrude(context, id + "F23", {"entities" : qUnion([Q0, Q1, Q2]), "operationType" : NewBodyOperationType.ADD, "depth" : 1.5 * mm});
        }
        {
            var Q0;
            Q0=makeQuery(id+"F21.opExtrude","CAP_FACE",FACE,{"disambiguationData":[OSD([sQuery(id+"F20.wireOp",EDGE,"E116"),sQuery(id+"F20.wireOp",EDGE,"E117"),sQuery(id+"F20.wireOp",EDGE,"E118"),sQuery(id+"F20.wireOp",EDGE,"E119.MirrorCS"),sQuery(id+"F20.wireOp",EDGE,"E120.MirrorCS"),sQuery(id+"F20.wireOp",EDGE,"E121.trimOffspring"),sQuery(id+"F20.wireOp",EDGE,"E122"),sQuery(id+"F20.wireOp",EDGE,"E124"),sQuery(id+"F20.wireOp",EDGE,"E125"),sQuery(id+"F20.wireOp",EDGE,"E128.MirrorCS")])],"isStart":true});
            var sketch = newSketch(context, id + "F24", { "sketchPlane" : qUnion([Q0])});
            skLineSegment(sketch, "E139.0", {"start": v(8.5, 4.7) * mm, "end": v(14.93, 0.2) * mm});
            skArc(sketch, "E140.0", {"start": v(4.99, 3.02) * mm, "mid": v(8.5, 4.13) * mm, "end": v(12.01, 3.02) * mm});
            skArc(sketch, "E141.0", {"start": v(6.7, 0.56) * mm, "mid": v(8.5, 1.13) * mm, "end": v(10.3, 0.56) * mm});
            skLineSegment(sketch, "E142", {"start": v(8.5, 4.13) * mm, "end": v(8.5, 1.13) * mm, "construction": true});
            skCircle(sketch, "E143", {"center": v(8.5, 2.63) * mm, "radius": 1.25 * mm});
            skSolve(sketch);
        }
        {
            var Q0;
            Q0=makeQuery(id+"F24.imprint","IMPRINT",FACE,{"disambiguationData":[TD([[makeQuery(id+"F24.imprint","IMPRINT",EDGE,{"derivedFrom":sQuery(id+"F24.wireOp",EDGE,"E143")}),1.0]])]});
            extrude(context, id + "F25", {"entities" : qUnion([Q0]), "operationType" : NewBodyOperationType.ADD, "depth" : 3.5 * mm});
        }
    });
